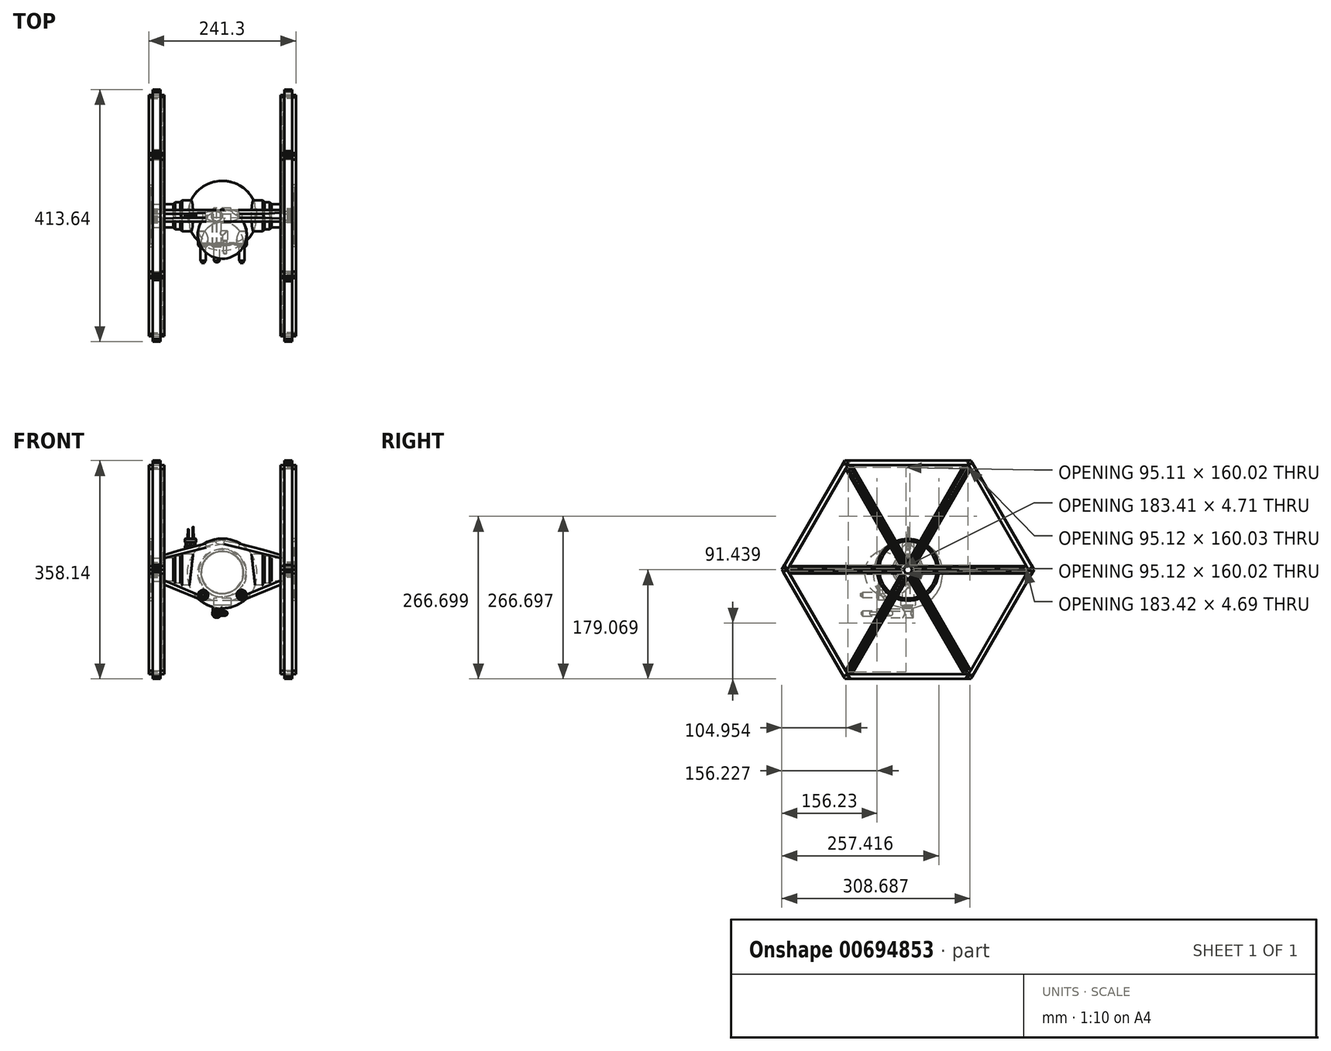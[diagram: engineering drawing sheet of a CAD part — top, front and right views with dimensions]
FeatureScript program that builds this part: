
annotation { "Feature Type Name" : "Feature", "Feature Type Description" : "" }
export const myFeature = defineFeature(function(context is Context, id is Id, definition is map)
    precondition{}
    {
        {
            var Q0;
            Q0=qCreatedBy(makeId("Right.planeOp"),FACE);
            var sketch = newSketch(context, id + "F0", { "sketchPlane" : qUnion([Q0])});
            skLineSegment(sketch, "E0", {"start": v(0, 51.2) * mm, "end": v(0, -63.1) * mm, "construction": true});
            skLineSegment(sketch, "E1", {"start": v(0, 51.2) * mm, "end": v(0, -63.1) * mm});
            skArc(sketch, "E2", {"start": v(0, 51.2) * mm, "mid": v(-57.2, -5.94) * mm, "end": v(0, -63.1) * mm});
            skSolve(sketch);
        }
        {
            var Q0;
            Q0=makeQuery(id+"F0.imprint","IMPRINT",FACE,{"disambiguationData":[TD([[makeQuery(id+"F0.imprint","IMPRINT",EDGE,{"derivedFrom":sQuery(id+"F0.wireOp",EDGE,"E1")}),-1.0]])]});
            var Q1;
            Q1=sQuery(id+"F0.wireOp",EDGE,"E1");
            revolve(context, id + "F1", {"entities" : qUnion([Q0]), "axis" : qUnion([Q1]), "revolveType" : RevolveType.FULL});
        }
        {
            var Q0;
            Q0=qCreatedBy(makeId("Right.planeOp"),FACE);
            var sketch = newSketch(context, id + "F2", { "sketchPlane" : qUnion([Q0])});
            skCircle(sketch, "E3", {"center": v(0, 0) * mm, "radius": 19.05 * mm});
            skSolve(sketch);
        }
        {
            var Q0;
            Q0 = qSketchRegion(id + "F2", true);
            extrude(context, id + "F3", {"entities" : qUnion([Q0]), "operationType" : NewBodyOperationType.ADD, "depth" : 203.2 * mm, "offsetDistance" : 25.4 * mm, "symmetric" : true});
        }
        {
            var Q0;
            Q0=makeQuery(id+"F3.opExtrude","CAP_FACE",FACE,{"disambiguationData":[OSD([sQuery(id+"F2.wireOp",EDGE,"E3")])],"isStart":false});
            var sketch = newSketch(context, id + "F4", { "sketchPlane" : qUnion([Q0])});
            skCircle(sketch, "E4.cCircle", {"center": v(0, 0) * mm, "radius": 171.45 * mm, "construction": true});
            skLineSegment(sketch, "E4.0", {"start": v(-98.99, 171.45) * mm, "end": v(98.99, 171.45) * mm});
            skLineSegment(sketch, "E4.1", {"start": v(98.99, 171.45) * mm, "end": v(197.97, 0) * mm});
            skLineSegment(sketch, "E4.2", {"start": v(197.97, 0) * mm, "end": v(98.99, -171.45) * mm});
            skLineSegment(sketch, "E4.3", {"start": v(98.99, -171.45) * mm, "end": v(-98.99, -171.45) * mm});
            skLineSegment(sketch, "E4.4", {"start": v(-98.99, -171.45) * mm, "end": v(-197.97, 0) * mm});
            skLineSegment(sketch, "E4.5", {"start": v(-197.97, 0) * mm, "end": v(-98.99, 171.45) * mm});
            skPoint(sketch, "E4.0.midPoint", {"position": v(0, 171.45) * mm});
            skSolve(sketch);
        }
        {
            var Q0;
            Q0 = qSketchRegion(id + "F4", true);
            extrude(context, id + "F5", {"entities" : qUnion([Q0]), "depth" : 12.7 * mm, "offsetDistance" : 25.4 * mm});
        }
        {
            var Q0;
            Q0=makeQuery(id+"F3.opExtrude","CAP_FACE",FACE,{"disambiguationData":[OSD([sQuery(id+"F2.wireOp",EDGE,"E3")])],"isStart":true});
            var sketch = newSketch(context, id + "F6", { "sketchPlane" : qUnion([Q0])});
            skCircle(sketch, "E5.cCircle", {"center": v(0, 0) * mm, "radius": 171.45 * mm, "construction": true});
            skLineSegment(sketch, "E5.0", {"start": v(-98.99, 171.45) * mm, "end": v(98.99, 171.45) * mm});
            skLineSegment(sketch, "E5.1", {"start": v(98.99, 171.45) * mm, "end": v(197.97, 0) * mm});
            skLineSegment(sketch, "E5.2", {"start": v(197.97, 0) * mm, "end": v(98.99, -171.45) * mm});
            skLineSegment(sketch, "E5.3", {"start": v(98.99, -171.45) * mm, "end": v(-98.99, -171.45) * mm});
            skLineSegment(sketch, "E5.4", {"start": v(-98.99, -171.45) * mm, "end": v(-197.97, 0) * mm});
            skLineSegment(sketch, "E5.5", {"start": v(-197.97, 0) * mm, "end": v(-98.99, 171.45) * mm});
            skPoint(sketch, "E5.0.midPoint", {"position": v(0, 171.45) * mm});
            skSolve(sketch);
        }
        {
            var Q0;
            Q0=makeQuery(id+"F6.imprint","IMPRINT",FACE,{"disambiguationData":[TD([[makeQuery(id+"F6.imprint","IMPRINT",EDGE,{"derivedFrom":sQuery(id+"F6.wireOp",EDGE,"E5.0")}),-1.0]])]});
            extrude(context, id + "F7", {"entities" : qUnion([Q0]), "depth" : 12.7 * mm, "offsetDistance" : 25.4 * mm});
        }
        {
            var Q0;
            Q0=makeQuery(id+"F3.opExtrude","CAP_FACE",FACE,{"disambiguationData":[OSD([sQuery(id+"F2.wireOp",EDGE,"E3")])],"isStart":true});
            extrude(context, id + "F8", {"entities" : qUnion([Q0]), "depth" : 12.7 * mm, "offsetDistance" : 25.4 * mm});
        }
        {
            var Q0;
            Q0=makeQuery(id+"F5.opExtrude","CAP_FACE",FACE,{"disambiguationData":[OSD([sQuery(id+"F4.wireOp",EDGE,"E4.0"),sQuery(id+"F4.wireOp",EDGE,"E4.1"),sQuery(id+"F4.wireOp",EDGE,"E4.2"),sQuery(id+"F4.wireOp",EDGE,"E4.3"),sQuery(id+"F4.wireOp",EDGE,"E4.4"),sQuery(id+"F4.wireOp",EDGE,"E4.5")])],"isStart":false});
            var sketch = newSketch(context, id + "F9", { "sketchPlane" : qUnion([Q0])});
            skCircle(sketch, "E6", {"center": v(0, 0) * mm, "radius": 19.05 * mm});
            skSolve(sketch);
        }
        {
            var Q0;
            Q0 = qSketchRegion(id + "F9", true);
            extrude(context, id + "F10", {"entities" : qUnion([Q0]), "operationType" : NewBodyOperationType.ADD, "depth" : 0.03 * mm, "offsetDistance" : 25.4 * mm});
        }
        {
            var Q0;
            Q0=qCreatedBy(makeId("Right.planeOp"),FACE);
            var sketch = newSketch(context, id + "F11", { "sketchPlane" : qUnion([Q0])});
            skCircle(sketch, "E7", {"center": v(0, 0) * mm, "radius": 25.4 * mm});
            skSolve(sketch);
        }
        {
            var Q0;
            Q0 = qSketchRegion(id + "F11", true);
            extrude(context, id + "F12", {"entities" : qUnion([Q0]), "operationType" : NewBodyOperationType.ADD, "depth" : 142.24 * mm, "offsetDistance" : 25.4 * mm, "symmetric" : true});
        }
        {
            var Q0;
            Q0=qCreatedBy(makeId("Right.planeOp"),FACE);
            var sketch = newSketch(context, id + "F13", { "sketchPlane" : qUnion([Q0])});
            skCircle(sketch, "E8", {"center": v(0, 0) * mm, "radius": 22.23 * mm});
            skSolve(sketch);
        }
        {
            var Q0;
            Q0 = qSketchRegion(id + "F13", true);
            extrude(context, id + "F14", {"entities" : qUnion([Q0]), "operationType" : NewBodyOperationType.ADD, "depth" : 165.1 * mm, "offsetDistance" : 25.4 * mm, "symmetric" : true});
        }
        {
            var Q0;
            Q0=makeQuery(id+"F10.opExtrude","CAP_FACE",FACE,{"disambiguationData":[OSD([sQuery(id+"F9.wireOp",EDGE,"E6")])],"isStart":false});
            var sketch = newSketch(context, id + "F15", { "sketchPlane" : qUnion([Q0])});
            skCircle(sketch, "E9", {"center": v(0, 0) * mm, "radius": 50.8 * mm});
            skSolve(sketch);
        }
        {
            var Q0;
            Q0 = qSketchRegion(id + "F15", true);
            extrude(context, id + "F16", {"entities" : qUnion([Q0]), "depth" : 8.9 * mm, "offsetDistance" : 25.4 * mm});
        }
        {
            var Q0;
            Q0=makeQuery(id+"F8.opExtrude","CAP_FACE",FACE,{"disambiguationData":[OSD([sQuery(id+"F2.wireOp",EDGE,"E3")])],"isStart":false});
            var sketch = newSketch(context, id + "F17", { "sketchPlane" : qUnion([Q0])});
            skCircle(sketch, "E10", {"center": v(0, 0) * mm, "radius": 50.8 * mm});
            skSolve(sketch);
        }
        {
            var Q0;
            Q0 = qSketchRegion(id + "F17", true);
            extrude(context, id + "F18", {"entities" : qUnion([Q0]), "depth" : 8.9 * mm, "offsetDistance" : 25.4 * mm});
        }
        {
            var Q0;
            Q0=makeQuery(id+"F7.opExtrude","CAP_FACE",FACE,{"disambiguationData":[OSD([sQuery(id+"F2.wireOp",EDGE,"E3"),sQuery(id+"F6.wireOp",EDGE,"E5.0"),sQuery(id+"F6.wireOp",EDGE,"E5.1"),sQuery(id+"F6.wireOp",EDGE,"E5.2"),sQuery(id+"F6.wireOp",EDGE,"E5.3"),sQuery(id+"F6.wireOp",EDGE,"E5.4"),sQuery(id+"F6.wireOp",EDGE,"E5.5")])],"isStart":false});
            var sketch = newSketch(context, id + "F19", { "sketchPlane" : qUnion([Q0])});
            skSolve(sketch);
        }
        {
            var Q0;
            Q0=makeQuery(id+"F19.imprint","IMPRINT",FACE,{"disambiguationData":[TD([[makeQuery(id+"F19.imprint","IMPRINT",EDGE,{"derivedFrom":makeQuery(id+"F7.opExtrude","CAP_EDGE",EDGE,{"disambiguationData":[OSD([sQuery(id+"F6.wireOp",EDGE,"E5.0")])],"isStart":false})}),-1.0]])]});
            var sketch = newSketch(context, id + "F20", { "sketchPlane" : qUnion([Q0])});
            skLineSegment(sketch, "E11", {"start": v(-98.99, 171.45) * mm, "end": v(-102.56, 165.29) * mm});
            skLineSegment(sketch, "E12", {"start": v(-98.99, 171.45) * mm, "end": v(-91.87, 171.45) * mm});
            skLineSegment(sketch, "E13", {"start": v(98.99, -171.45) * mm, "end": v(102.55, -165.29) * mm});
            skLineSegment(sketch, "E14", {"start": v(98.99, -171.45) * mm, "end": v(91.87, -171.45) * mm});
            skLineSegment(sketch, "E15", {"start": v(91.87, -171.45) * mm, "end": v(-102.56, 165.29) * mm});
            skLineSegment(sketch, "E16", {"start": v(-91.87, 171.45) * mm, "end": v(102.55, -165.29) * mm});
            skLineSegment(sketch, "E17", {"start": v(98.99, 171.45) * mm, "end": v(91.87, 171.45) * mm});
            skLineSegment(sketch, "E18", {"start": v(98.99, 171.45) * mm, "end": v(102.55, 165.29) * mm});
            skLineSegment(sketch, "E19", {"start": v(-98.99, -171.45) * mm, "end": v(-102.54, -165.29) * mm});
            skLineSegment(sketch, "E20", {"start": v(-98.99, -171.45) * mm, "end": v(-91.87, -171.45) * mm});
            skLineSegment(sketch, "E21", {"start": v(-91.87, -171.45) * mm, "end": v(102.55, 165.29) * mm});
            skLineSegment(sketch, "E22", {"start": v(91.87, 171.45) * mm, "end": v(-102.54, -165.29) * mm});
            skLineSegment(sketch, "E23", {"start": v(197.97, 0) * mm, "end": v(194.4, 6.16) * mm});
            skLineSegment(sketch, "E24", {"start": v(197.97, 0) * mm, "end": v(194.43, -6.16) * mm});
            skLineSegment(sketch, "E25", {"start": v(-197.98, 0) * mm, "end": v(-194.43, 6.15) * mm});
            skLineSegment(sketch, "E26", {"start": v(-197.98, 0) * mm, "end": v(-194.42, -6.15) * mm});
            skLineSegment(sketch, "E27", {"start": v(-194.43, 6.15) * mm, "end": v(194.4, 6.16) * mm});
            skLineSegment(sketch, "E28", {"start": v(194.43, -6.16) * mm, "end": v(-194.42, -6.15) * mm});
            skSolve(sketch);
        }
        {
            var Q0;
            Q0 = qSketchRegion(id + "F20", true);
            extrude(context, id + "F21", {"entities" : qUnion([Q0]), "depth" : 38.1 * mm, "offsetDistance" : 25.4 * mm, "symmetric" : true});
        }
        {
            var Q0;
            Q0=makeQuery(id+"F5.opExtrude","CAP_FACE",FACE,{"disambiguationData":[OSD([sQuery(id+"F4.wireOp",EDGE,"E4.0"),sQuery(id+"F4.wireOp",EDGE,"E4.1"),sQuery(id+"F4.wireOp",EDGE,"E4.2"),sQuery(id+"F4.wireOp",EDGE,"E4.3"),sQuery(id+"F4.wireOp",EDGE,"E4.4"),sQuery(id+"F4.wireOp",EDGE,"E4.5")])],"isStart":false});
            var sketch = newSketch(context, id + "F22", { "sketchPlane" : qUnion([Q0])});
            skLineSegment(sketch, "E29", {"start": v(-98.99, 171.45) * mm, "end": v(-102.54, 165.3) * mm});
            skLineSegment(sketch, "E30", {"start": v(-98.99, 171.45) * mm, "end": v(-91.87, 171.45) * mm});
            skLineSegment(sketch, "E31", {"start": v(98.99, 171.45) * mm, "end": v(91.88, 171.45) * mm});
            skLineSegment(sketch, "E32", {"start": v(98.99, 171.45) * mm, "end": v(102.55, 165.28) * mm});
            skLineSegment(sketch, "E33", {"start": v(197.97, 0) * mm, "end": v(194.42, 6.16) * mm});
            skLineSegment(sketch, "E34", {"start": v(197.97, 0) * mm, "end": v(194.42, -6.16) * mm});
            skLineSegment(sketch, "E35", {"start": v(98.99, -171.45) * mm, "end": v(102.54, -165.29) * mm});
            skLineSegment(sketch, "E36", {"start": v(98.99, -171.45) * mm, "end": v(91.86, -171.45) * mm});
            skLineSegment(sketch, "E37", {"start": v(-98.99, -171.45) * mm, "end": v(-91.88, -171.45) * mm});
            skLineSegment(sketch, "E38", {"start": v(-98.99, -171.45) * mm, "end": v(-102.54, -165.3) * mm});
            skLineSegment(sketch, "E39", {"start": v(-197.97, 0) * mm, "end": v(-194.42, 6.16) * mm});
            skLineSegment(sketch, "E40", {"start": v(-197.97, 0) * mm, "end": v(-194.42, -6.16) * mm});
            skLineSegment(sketch, "E41", {"start": v(-194.42, -6.16) * mm, "end": v(194.42, -6.16) * mm});
            skLineSegment(sketch, "E42", {"start": v(194.42, 6.16) * mm, "end": v(-194.42, 6.16) * mm});
            skLineSegment(sketch, "E43", {"start": v(-102.54, 165.3) * mm, "end": v(91.86, -171.45) * mm});
            skLineSegment(sketch, "E44", {"start": v(-91.87, 171.45) * mm, "end": v(102.54, -165.29) * mm});
            skLineSegment(sketch, "E45", {"start": v(91.88, 171.45) * mm, "end": v(-102.54, -165.3) * mm});
            skLineSegment(sketch, "E46", {"start": v(102.55, 165.28) * mm, "end": v(-91.88, -171.45) * mm});
            skSolve(sketch);
        }
        {
            var Q0;
            Q0 = qSketchRegion(id + "F22", true);
            extrude(context, id + "F23", {"entities" : qUnion([Q0]), "depth" : 38.1 * mm, "offsetDistance" : 25.4 * mm, "symmetric" : true});
        }
        {
            var Q0;
            Q0=makeQuery(id+"F23.opExtrude","CAP_FACE",FACE,{"disambiguationData":[OSD([sQuery(id+"F22.wireOp",EDGE,"E29"),sQuery(id+"F22.wireOp",EDGE,"E30"),sQuery(id+"F22.wireOp",EDGE,"E31"),sQuery(id+"F22.wireOp",EDGE,"E32"),sQuery(id+"F22.wireOp",EDGE,"E33"),sQuery(id+"F22.wireOp",EDGE,"E34"),sQuery(id+"F22.wireOp",EDGE,"E35"),sQuery(id+"F22.wireOp",EDGE,"E36"),sQuery(id+"F22.wireOp",EDGE,"E37"),sQuery(id+"F22.wireOp",EDGE,"E38"),sQuery(id+"F22.wireOp",EDGE,"E39"),sQuery(id+"F22.wireOp",EDGE,"E40"),sQuery(id+"F22.wireOp",EDGE,"E41"),sQuery(id+"F22.wireOp",EDGE,"E42"),sQuery(id+"F22.wireOp",EDGE,"E43"),sQuery(id+"F22.wireOp",EDGE,"E44"),sQuery(id+"F22.wireOp",EDGE,"E45"),sQuery(id+"F22.wireOp",EDGE,"E46")])],"isStart":false});
            var sketch = newSketch(context, id + "F24", { "sketchPlane" : qUnion([Q0])});
            skLineSegment(sketch, "E47.bottom", {"start": v(-254.73, 221.4) * mm, "end": v(358.63, 221.4) * mm});
            skLineSegment(sketch, "E47.top", {"start": v(-254.73, -186.2) * mm, "end": v(358.63, -186.2) * mm});
            skLineSegment(sketch, "E47.left", {"start": v(-254.73, 221.4) * mm, "end": v(-254.73, -186.2) * mm});
            skLineSegment(sketch, "E47.right", {"start": v(358.63, 221.4) * mm, "end": v(358.63, -186.2) * mm});
            skSolve(sketch);
        }
        {
            var Q0;
            Q0 = qSketchRegion(id + "F24", true);
            extrude(context, id + "F25", {"entities" : qUnion([Q0]), "operationType" : NewBodyOperationType.REMOVE, "depth" : 25.4 * mm, "offsetDistance" : 25.4 * mm, "symmetric" : true});
        }
        {
            var Q0;
            Q0=makeQuery(id+"F21.opExtrude","CAP_FACE",FACE,{"disambiguationData":[OSD([sQuery(id+"F20.wireOp",EDGE,"E11"),sQuery(id+"F20.wireOp",EDGE,"E12"),sQuery(id+"F20.wireOp",EDGE,"E13"),sQuery(id+"F20.wireOp",EDGE,"E14"),sQuery(id+"F20.wireOp",EDGE,"E15"),sQuery(id+"F20.wireOp",EDGE,"E16"),sQuery(id+"F20.wireOp",EDGE,"E17"),sQuery(id+"F20.wireOp",EDGE,"E18"),sQuery(id+"F20.wireOp",EDGE,"E19"),sQuery(id+"F20.wireOp",EDGE,"E20"),sQuery(id+"F20.wireOp",EDGE,"E21"),sQuery(id+"F20.wireOp",EDGE,"E22"),sQuery(id+"F20.wireOp",EDGE,"E23"),sQuery(id+"F20.wireOp",EDGE,"E24"),sQuery(id+"F20.wireOp",EDGE,"E25"),sQuery(id+"F20.wireOp",EDGE,"E26"),sQuery(id+"F20.wireOp",EDGE,"E27"),sQuery(id+"F20.wireOp",EDGE,"E28")])],"isStart":false});
            var sketch = newSketch(context, id + "F26", { "sketchPlane" : qUnion([Q0])});
            skLineSegment(sketch, "E48.bottom", {"start": v(-248.69, 213.9) * mm, "end": v(348.05, 213.9) * mm});
            skLineSegment(sketch, "E48.top", {"start": v(-248.69, -200.94) * mm, "end": v(348.05, -200.94) * mm});
            skLineSegment(sketch, "E48.left", {"start": v(-248.69, 213.9) * mm, "end": v(-248.69, -200.94) * mm});
            skLineSegment(sketch, "E48.right", {"start": v(348.05, 213.9) * mm, "end": v(348.05, -200.94) * mm});
            skSolve(sketch);
        }
        {
            var Q0;
            Q0 = qSketchRegion(id + "F26", true);
            extrude(context, id + "F27", {"entities" : qUnion([Q0]), "operationType" : NewBodyOperationType.REMOVE, "depth" : 25.4 * mm, "offsetDistance" : 25.4 * mm, "symmetric" : true});
        }
        {
            var Q0;
            Q0=makeQuery(id+"F7.opExtrude","SWEPT_FACE",FACE,{"disambiguationData":[OSD([sQuery(id+"F6.wireOp",EDGE,"E5.0")])]});
            var sketch = newSketch(context, id + "F28", { "sketchPlane" : qUnion([Q0])});
            skLineSegment(sketch, "E49.bottom", {"start": v(-114.3, 98.99) * mm, "end": v(-101.6, 98.99) * mm});
            skLineSegment(sketch, "E49.top", {"start": v(-114.3, -98.99) * mm, "end": v(-101.6, -98.99) * mm});
            skLineSegment(sketch, "E49.left", {"start": v(-114.3, 98.99) * mm, "end": v(-114.3, -98.99) * mm});
            skLineSegment(sketch, "E49.right", {"start": v(-101.6, 98.99) * mm, "end": v(-101.6, -98.99) * mm});
            skLineSegment(sketch, "E50.bottom", {"start": v(101.63, 98.98) * mm, "end": v(114.3, 98.98) * mm});
            skLineSegment(sketch, "E50.top", {"start": v(101.63, -98.98) * mm, "end": v(114.3, -98.98) * mm});
            skLineSegment(sketch, "E50.left", {"start": v(101.63, 98.98) * mm, "end": v(101.63, -98.98) * mm});
            skLineSegment(sketch, "E50.right", {"start": v(114.3, 98.98) * mm, "end": v(114.3, -98.98) * mm});
            skSolve(sketch);
        }
        {
            var Q0;
            Q0=makeQuery(id+"F7.opExtrude","SWEPT_FACE",FACE,{"disambiguationData":[OSD([sQuery(id+"F6.wireOp",EDGE,"E5.5")])]});
            var sketch = newSketch(context, id + "F29", { "sketchPlane" : qUnion([Q0])});
            skLineSegment(sketch, "E51.bottom", {"start": v(114.3, -98.99) * mm, "end": v(101.6, -98.99) * mm});
            skLineSegment(sketch, "E51.top", {"start": v(114.3, 98.99) * mm, "end": v(101.6, 98.99) * mm});
            skLineSegment(sketch, "E51.left", {"start": v(114.3, -98.99) * mm, "end": v(114.3, 98.99) * mm});
            skLineSegment(sketch, "E51.right", {"start": v(101.6, -98.99) * mm, "end": v(101.6, 98.99) * mm});
            skLineSegment(sketch, "E52.bottom", {"start": v(-101.59, -98.99) * mm, "end": v(-114.27, -98.99) * mm});
            skLineSegment(sketch, "E52.top", {"start": v(-101.59, 98.99) * mm, "end": v(-114.27, 98.99) * mm});
            skLineSegment(sketch, "E52.left", {"start": v(-101.59, -98.99) * mm, "end": v(-101.59, 98.99) * mm});
            skLineSegment(sketch, "E52.right", {"start": v(-114.27, -98.99) * mm, "end": v(-114.27, 98.99) * mm});
            skSolve(sketch);
        }
        {
            var Q0;
            Q0=makeQuery(id+"F5.opExtrude","SWEPT_FACE",FACE,{"disambiguationData":[OSD([sQuery(id+"F4.wireOp",EDGE,"E4.2")])]});
            var sketch = newSketch(context, id + "F30", { "sketchPlane" : qUnion([Q0])});
            skLineSegment(sketch, "E53.bottom", {"start": v(-114.3, 98.99) * mm, "end": v(-101.6, 98.99) * mm});
            skLineSegment(sketch, "E53.top", {"start": v(-114.3, -98.99) * mm, "end": v(-101.6, -98.99) * mm});
            skLineSegment(sketch, "E53.left", {"start": v(-114.3, 98.99) * mm, "end": v(-114.3, -98.99) * mm});
            skLineSegment(sketch, "E53.right", {"start": v(-101.6, 98.99) * mm, "end": v(-101.6, -98.99) * mm});
            skLineSegment(sketch, "E54.bottom", {"start": v(101.59, 98.99) * mm, "end": v(114.3, 98.99) * mm});
            skLineSegment(sketch, "E54.top", {"start": v(101.59, -98.99) * mm, "end": v(114.3, -98.99) * mm});
            skLineSegment(sketch, "E54.left", {"start": v(101.59, 98.99) * mm, "end": v(101.59, -98.99) * mm});
            skLineSegment(sketch, "E54.right", {"start": v(114.3, 98.99) * mm, "end": v(114.3, -98.99) * mm});
            skSolve(sketch);
        }
        {
            var Q0;
            Q0=makeQuery(id+"F7.opExtrude","SWEPT_FACE",FACE,{"disambiguationData":[OSD([sQuery(id+"F6.wireOp",EDGE,"E5.3")])]});
            var sketch = newSketch(context, id + "F31", { "sketchPlane" : qUnion([Q0])});
            skLineSegment(sketch, "E55.bottom", {"start": v(-114.3, 98.99) * mm, "end": v(-101.6, 98.99) * mm});
            skLineSegment(sketch, "E55.top", {"start": v(-114.3, -98.99) * mm, "end": v(-101.6, -98.99) * mm});
            skLineSegment(sketch, "E55.left", {"start": v(-114.3, 98.99) * mm, "end": v(-114.3, -98.99) * mm});
            skLineSegment(sketch, "E55.right", {"start": v(-101.6, 98.99) * mm, "end": v(-101.6, -98.99) * mm});
            skLineSegment(sketch, "E56.bottom", {"start": v(101.62, 98.99) * mm, "end": v(114.3, 98.99) * mm});
            skLineSegment(sketch, "E56.top", {"start": v(101.62, -98.99) * mm, "end": v(114.3, -98.99) * mm});
            skLineSegment(sketch, "E56.left", {"start": v(101.62, 98.99) * mm, "end": v(101.62, -98.99) * mm});
            skLineSegment(sketch, "E56.right", {"start": v(114.3, 98.99) * mm, "end": v(114.3, -98.99) * mm});
            skSolve(sketch);
        }
        {
            var Q0;
            Q0=makeQuery(id+"F7.opExtrude","SWEPT_FACE",FACE,{"disambiguationData":[OSD([sQuery(id+"F6.wireOp",EDGE,"E5.2")])]});
            var sketch = newSketch(context, id + "F32", { "sketchPlane" : qUnion([Q0])});
            skLineSegment(sketch, "E57.bottom", {"start": v(-114.3, 98.99) * mm, "end": v(-101.6, 98.99) * mm});
            skLineSegment(sketch, "E57.top", {"start": v(-114.3, -98.99) * mm, "end": v(-101.6, -98.99) * mm});
            skLineSegment(sketch, "E57.left", {"start": v(-114.3, 98.99) * mm, "end": v(-114.3, -98.99) * mm});
            skLineSegment(sketch, "E57.right", {"start": v(-101.6, 98.99) * mm, "end": v(-101.6, -98.99) * mm});
            skLineSegment(sketch, "E58.bottom", {"start": v(101.6, 98.99) * mm, "end": v(114.3, 98.99) * mm});
            skLineSegment(sketch, "E58.top", {"start": v(101.6, -98.99) * mm, "end": v(114.3, -98.99) * mm});
            skLineSegment(sketch, "E58.left", {"start": v(101.6, 98.99) * mm, "end": v(101.6, -98.99) * mm});
            skLineSegment(sketch, "E58.right", {"start": v(114.3, 98.99) * mm, "end": v(114.3, -98.99) * mm});
            skSolve(sketch);
        }
        {
            var Q0;
            Q0=makeQuery(id+"F7.opExtrude","SWEPT_FACE",FACE,{"disambiguationData":[OSD([sQuery(id+"F6.wireOp",EDGE,"E5.1")])]});
            var sketch = newSketch(context, id + "F33", { "sketchPlane" : qUnion([Q0])});
            skLineSegment(sketch, "E59.bottom", {"start": v(-114.3, 98.99) * mm, "end": v(-101.6, 98.99) * mm});
            skLineSegment(sketch, "E59.top", {"start": v(-114.3, -98.99) * mm, "end": v(-101.6, -98.99) * mm});
            skLineSegment(sketch, "E59.left", {"start": v(-114.3, 98.99) * mm, "end": v(-114.3, -98.99) * mm});
            skLineSegment(sketch, "E59.right", {"start": v(-101.6, 98.99) * mm, "end": v(-101.6, -98.99) * mm});
            skLineSegment(sketch, "E60.bottom", {"start": v(101.61, 98.99) * mm, "end": v(114.37, 98.99) * mm});
            skLineSegment(sketch, "E60.top", {"start": v(101.61, -98.99) * mm, "end": v(114.37, -98.99) * mm});
            skLineSegment(sketch, "E60.left", {"start": v(101.61, 98.99) * mm, "end": v(101.61, -98.99) * mm});
            skLineSegment(sketch, "E60.right", {"start": v(114.37, 98.99) * mm, "end": v(114.37, -98.99) * mm});
            skSolve(sketch);
        }
        {
            var Q0;
            Q0 = qSketchRegion(id + "F33", true);
            extrude(context, id + "F34", {"entities" : qUnion([Q0]), "depth" : 7.62 * mm, "offsetDistance" : 25.4 * mm});
        }
        {
            var Q0;
            Q0 = qSketchRegion(id + "F32", true);
            extrude(context, id + "F35", {"entities" : qUnion([Q0]), "depth" : 7.62 * mm, "offsetDistance" : 25.4 * mm});
        }
        {
            var Q0;
            Q0 = qSketchRegion(id + "F31", true);
            extrude(context, id + "F36", {"entities" : qUnion([Q0]), "depth" : 7.62 * mm, "offsetDistance" : 25.4 * mm});
        }
        {
            var Q0;
            Q0 = qSketchRegion(id + "F30", true);
            extrude(context, id + "F37", {"entities" : qUnion([Q0]), "depth" : 7.62 * mm, "offsetDistance" : 25.4 * mm});
        }
        {
            var Q0;
            Q0 = qSketchRegion(id + "F29", true);
            extrude(context, id + "F38", {"entities" : qUnion([Q0]), "depth" : 7.62 * mm, "offsetDistance" : 25.4 * mm});
        }
        {
            var Q0;
            Q0 = qSketchRegion(id + "F28", true);
            extrude(context, id + "F39", {"entities" : qUnion([Q0]), "depth" : 7.62 * mm, "offsetDistance" : 25.4 * mm});
        }
        {
            var Q0;
            Q0=qCreatedBy(makeId("Front.planeOp"),FACE);
            cPlane(context, id + "F40", {"entities" : qUnion([Q0]), "cplaneType" : CPlaneType.OFFSET, "offset" : 38.1 * mm, "width" : 152.4 * mm, "height" : 152.4 * mm});
        }
        {
            var Q0;
            Q0=qCreatedBy(id+"F40.planeOp",FACE);
            var sketch = newSketch(context, id + "F41", { "sketchPlane" : qUnion([Q0])});
            skCircle(sketch, "E61", {"center": v(-31.2, -41.21) * mm, "radius": 8.26 * mm});
            skCircle(sketch, "E62", {"center": v(31.77, -41.21) * mm, "radius": 8.26 * mm});
            skSolve(sketch);
        }
        {
            var Q0;
            Q0 = qSketchRegion(id + "F41", true);
            extrude(context, id + "F42", {"entities" : qUnion([Q0]), "operationType" : NewBodyOperationType.ADD, "depth" : 25.4 * mm, "offsetDistance" : 25.4 * mm, "symmetric" : true});
        }
        {
            var Q0;
            Q0=makeQuery(id+"F42.opExtrude","CAP_FACE",FACE,{"disambiguationData":[OSD([sQuery(id+"F41.wireOp",EDGE,"E61")])],"isStart":false});
            var sketch = newSketch(context, id + "F43", { "sketchPlane" : qUnion([Q0])});
            skCircle(sketch, "E63", {"center": v(-31.2, -41.21) * mm, "radius": 4.45 * mm});
            skSolve(sketch);
        }
        {
            var Q0;
            Q0=makeQuery(id+"F42.opExtrude","CAP_FACE",FACE,{"disambiguationData":[OSD([sQuery(id+"F41.wireOp",EDGE,"E62")])],"isStart":false});
            var sketch = newSketch(context, id + "F44", { "sketchPlane" : qUnion([Q0])});
            skCircle(sketch, "E64", {"center": v(31.77, -41.21) * mm, "radius": 4.45 * mm});
            skSolve(sketch);
        }
        {
            var Q0;
            Q0 = qSketchRegion(id + "F44", true);
            extrude(context, id + "F45", {"entities" : qUnion([Q0]), "operationType" : NewBodyOperationType.ADD, "depth" : 25.4 * mm, "offsetDistance" : 25.4 * mm});
        }
        {
            var Q0;
            Q0 = qSketchRegion(id + "F43", true);
            extrude(context, id + "F46", {"entities" : qUnion([Q0]), "operationType" : NewBodyOperationType.ADD, "depth" : 25.4 * mm, "offsetDistance" : 25.4 * mm});
        }
        {
            var Q0;
            Q0=makeQuery(id+"F46.opExtrude","CAP_FACE",FACE,{"disambiguationData":[OSD([sQuery(id+"F43.wireOp",EDGE,"E63")])],"isStart":false});
            var sketch = newSketch(context, id + "F47", { "sketchPlane" : qUnion([Q0])});
            skCircle(sketch, "E65", {"center": v(-31.2, -41.21) * mm, "radius": 2.54 * mm});
            skSolve(sketch);
        }
        {
            var Q0;
            Q0=makeQuery(id+"F45.opExtrude","CAP_FACE",FACE,{"disambiguationData":[OSD([sQuery(id+"F44.wireOp",EDGE,"E64")])],"isStart":false});
            var sketch = newSketch(context, id + "F48", { "sketchPlane" : qUnion([Q0])});
            skCircle(sketch, "E66", {"center": v(31.77, -41.21) * mm, "radius": 2.54 * mm});
            skSolve(sketch);
        }
        {
            var Q0;
            Q0 = qSketchRegion(id + "F48", true);
            var Q1;
            Q1=makeQuery(id+"F47.imprint","IMPRINT",FACE,{"disambiguationData":[TD([[makeQuery(id+"F47.imprint","IMPRINT",EDGE,{"derivedFrom":sQuery(id+"F47.wireOp",EDGE,"E65")}),1.0]])]});
            extrude(context, id + "F49", {"entities" : qUnion([Q0, Q1]), "depth" : 1.27 * mm, "offsetDistance" : 25.4 * mm});
        }
        {
            var Q0;
            Q0=makeQuery(id+"F42.opExtrude","CAP_EDGE",EDGE,{"disambiguationData":[OSD([sQuery(id+"F41.wireOp",EDGE,"E61")])],"isStart":false});
            var Q1;
            Q1=makeQuery(id+"F46.opExtrude","CAP_EDGE",EDGE,{"disambiguationData":[OSD([sQuery(id+"F43.wireOp",EDGE,"E63")])],"isStart":false});
            var Q2;
            Q2=makeQuery(id+"F42.opExtrude","CAP_EDGE",EDGE,{"disambiguationData":[OSD([sQuery(id+"F41.wireOp",EDGE,"E62")])],"isStart":false});
            var Q3;
            Q3=makeQuery(id+"F45.opExtrude","CAP_EDGE",EDGE,{"disambiguationData":[OSD([sQuery(id+"F44.wireOp",EDGE,"E64")])],"isStart":false});
            chamfer(context, id + "F50", {"entities" : qUnion([Q0, Q1, Q2, Q3]), "width" : 2.54 * mm, "tangentPropagation" : true});
        }
        {
            var Q0;
            Q0=qCreatedBy(makeId("Front.planeOp"),FACE);
            var sketch = newSketch(context, id + "F51", { "sketchPlane" : qUnion([Q0])});
            skLineSegment(sketch, "E67.bottom", {"start": v(0, 50.8) * mm, "end": v(-95.25, 50.8) * mm});
            skLineSegment(sketch, "E67.top", {"start": v(0, 0) * mm, "end": v(-95.25, 0) * mm});
            skLineSegment(sketch, "E67.left", {"start": v(0, 50.8) * mm, "end": v(0, 0) * mm});
            skLineSegment(sketch, "E67.right", {"start": v(-95.25, 50.8) * mm, "end": v(-95.25, 0) * mm});
            skLineSegment(sketch, "E68.bottom", {"start": v(0, 0) * mm, "end": v(95.25, 0) * mm});
            skLineSegment(sketch, "E68.top", {"start": v(0, 50.8) * mm, "end": v(95.25, 50.8) * mm});
            skLineSegment(sketch, "E68.left", {"start": v(0, 0) * mm, "end": v(0, 50.8) * mm});
            skLineSegment(sketch, "E68.right", {"start": v(95.25, 0) * mm, "end": v(95.25, 50.8) * mm});
            skLineSegment(sketch, "E69.top", {"start": v(0, -50.8) * mm, "end": v(-95.25, -50.8) * mm});
            skLineSegment(sketch, "E69.left", {"start": v(0, 0) * mm, "end": v(0, -50.8) * mm});
            skLineSegment(sketch, "E69.right", {"start": v(-95.25, 0) * mm, "end": v(-95.25, -50.8) * mm});
            skLineSegment(sketch, "E70.top", {"start": v(0, -50.8) * mm, "end": v(95.25, -50.8) * mm});
            skLineSegment(sketch, "E70.right", {"start": v(95.25, 0) * mm, "end": v(95.25, -50.8) * mm});
            skSolve(sketch);
        }
        {
            var Q0;
            Q0 = qSketchRegion(id + "F51", true);
            extrude(context, id + "F52", {"entities" : qUnion([Q0]), "depth" : 19.05 * mm, "offsetDistance" : 25.4 * mm, "symmetric" : true});
        }
        {
            var Q0;
            Q0=makeQuery(id+"F52.opExtrude","SWEPT_EDGE",EDGE,{"disambiguationData":[OSD([sQuery(id+"F51.wireOp",EDGE,"E67.bottom"),sQuery(id+"F51.wireOp",EDGE,"E67.right")])]});
            var Q1;
            Q1=makeQuery(id+"F52.opExtrude","SWEPT_EDGE",EDGE,{"disambiguationData":[OSD([sQuery(id+"F51.wireOp",EDGE,"E68.top"),sQuery(id+"F51.wireOp",EDGE,"E68.right")])]});
            var Q2;
            Q2=makeQuery(id+"F52.opExtrude","SWEPT_EDGE",EDGE,{"disambiguationData":[OSD([sQuery(id+"F51.wireOp",EDGE,"E69.top"),sQuery(id+"F51.wireOp",EDGE,"E69.right")])]});
            var Q3;
            Q3=makeQuery(id+"F52.opExtrude","SWEPT_EDGE",EDGE,{"disambiguationData":[OSD([sQuery(id+"F51.wireOp",EDGE,"E70.top"),sQuery(id+"F51.wireOp",EDGE,"E70.right")])]});
            chamfer(context, id + "F53", {"entities" : qUnion([Q0, Q1, Q2, Q3]), "width" : 25.4 * mm, "tangentPropagation" : true});
        }
        {
            var Q0;
            {var subQ0=sQuery(id+"F51.wireOp",EDGE,"E67.bottom");Q0=makeQuery(id+"F53.opChamfer","BLEND_EDGE",EDGE,{"blendedFrom":[makeQuery(id+"F52.opExtrude","SWEPT_EDGE",EDGE,{"disambiguationData":[OSD([subQ0,sQuery(id+"F51.wireOp",EDGE,"E67.right")])]}),makeQuery(id+"F52.opExtrude","SWEPT_FACE",FACE,{"disambiguationData":[OSD([subQ0,sQuery(id+"F51.wireOp",EDGE,"E68.top")])]})],"blendedInto":[makeQuery(id+"F52.opExtrude","SWEPT_FACE",FACE,{"disambiguationData":[OSD([subQ0,sQuery(id+"F51.wireOp",EDGE,"E68.top")])]})]});}
            var Q1;
            {var subQ0=sQuery(id+"F51.wireOp",EDGE,"E68.top");Q1=makeQuery(id+"F53.opChamfer","BLEND_EDGE",EDGE,{"blendedFrom":[makeQuery(id+"F52.opExtrude","SWEPT_EDGE",EDGE,{"disambiguationData":[OSD([subQ0,sQuery(id+"F51.wireOp",EDGE,"E68.right")])]}),makeQuery(id+"F52.opExtrude","SWEPT_FACE",FACE,{"disambiguationData":[OSD([sQuery(id+"F51.wireOp",EDGE,"E67.bottom"),subQ0])]})],"blendedInto":[makeQuery(id+"F52.opExtrude","SWEPT_FACE",FACE,{"disambiguationData":[OSD([sQuery(id+"F51.wireOp",EDGE,"E67.bottom"),subQ0])]})]});}
            var Q2;
            {var subQ0=sQuery(id+"F51.wireOp",EDGE,"E69.top");Q2=makeQuery(id+"F53.opChamfer","BLEND_EDGE",EDGE,{"blendedFrom":[makeQuery(id+"F52.opExtrude","SWEPT_EDGE",EDGE,{"disambiguationData":[OSD([subQ0,sQuery(id+"F51.wireOp",EDGE,"E69.right")])]}),makeQuery(id+"F52.opExtrude","SWEPT_FACE",FACE,{"disambiguationData":[OSD([subQ0,sQuery(id+"F51.wireOp",EDGE,"E70.top")])]})],"blendedInto":[makeQuery(id+"F52.opExtrude","SWEPT_FACE",FACE,{"disambiguationData":[OSD([subQ0,sQuery(id+"F51.wireOp",EDGE,"E70.top")])]})]});}
            var Q3;
            {var subQ0=sQuery(id+"F51.wireOp",EDGE,"E70.top");Q3=makeQuery(id+"F53.opChamfer","BLEND_EDGE",EDGE,{"blendedFrom":[makeQuery(id+"F52.opExtrude","SWEPT_EDGE",EDGE,{"disambiguationData":[OSD([subQ0,sQuery(id+"F51.wireOp",EDGE,"E70.right")])]}),makeQuery(id+"F52.opExtrude","SWEPT_FACE",FACE,{"disambiguationData":[OSD([sQuery(id+"F51.wireOp",EDGE,"E69.top"),subQ0])]})],"blendedInto":[makeQuery(id+"F52.opExtrude","SWEPT_FACE",FACE,{"disambiguationData":[OSD([sQuery(id+"F51.wireOp",EDGE,"E69.top"),subQ0])]})]});}
            chamfer(context, id + "F54", {"entities" : qUnion([Q0, Q1, Q2, Q3]), "width" : 38.1 * mm, "tangentPropagation" : true});
        }
        {
            var Q0;
            {var subQ0=sQuery(id+"F51.wireOp",EDGE,"E67.bottom");var subQ1=makeQuery(id+"F52.opExtrude","SWEPT_FACE",FACE,{"disambiguationData":[OSD([subQ0,sQuery(id+"F51.wireOp",EDGE,"E68.top")])]});Q0=makeQuery(id+"F54.opChamfer","BLEND_EDGE",EDGE,{"blendedFrom":[makeQuery(id+"F53.opChamfer","BLEND_EDGE",EDGE,{"blendedFrom":[makeQuery(id+"F52.opExtrude","SWEPT_EDGE",EDGE,{"disambiguationData":[OSD([subQ0,sQuery(id+"F51.wireOp",EDGE,"E67.right")])]}),subQ1],"blendedInto":[subQ1]}),subQ1],"blendedInto":[subQ1]});}
            var Q1;
            {var subQ0=sQuery(id+"F51.wireOp",EDGE,"E68.top");var subQ1=makeQuery(id+"F52.opExtrude","SWEPT_FACE",FACE,{"disambiguationData":[OSD([sQuery(id+"F51.wireOp",EDGE,"E67.bottom"),subQ0])]});Q1=makeQuery(id+"F54.opChamfer","BLEND_EDGE",EDGE,{"blendedFrom":[makeQuery(id+"F53.opChamfer","BLEND_EDGE",EDGE,{"blendedFrom":[makeQuery(id+"F52.opExtrude","SWEPT_EDGE",EDGE,{"disambiguationData":[OSD([subQ0,sQuery(id+"F51.wireOp",EDGE,"E68.right")])]}),subQ1],"blendedInto":[subQ1]}),subQ1],"blendedInto":[subQ1]});}
            chamfer(context, id + "F55", {"entities" : qUnion([Q0, Q1]), "width" : 44.45 * mm, "tangentPropagation" : true});
        }
        {
            var Q0;
            {var subQ0=sQuery(id+"F51.wireOp",EDGE,"E68.top");var subQ1=sQuery(id+"F51.wireOp",EDGE,"E67.right");var subQ2=sQuery(id+"F51.wireOp",EDGE,"E67.bottom");var subQ3=makeQuery(id+"F52.opExtrude","SWEPT_FACE",FACE,{"disambiguationData":[OSD([subQ2,subQ0])]});Q0=makeQuery(id+"F55.opChamfer","BLEND_EDGE",EDGE,{"blendedFrom":[makeQuery(id+"F54.opChamfer","BLEND_EDGE",EDGE,{"blendedFrom":[makeQuery(id+"F53.opChamfer","BLEND_EDGE",EDGE,{"blendedFrom":[makeQuery(id+"F52.opExtrude","SWEPT_EDGE",EDGE,{"disambiguationData":[OSD([subQ2,subQ1])]}),subQ3],"blendedInto":[subQ3]}),subQ3],"blendedInto":[subQ3]}),makeQuery(id+"F54.opChamfer","BLEND_FACE",FACE,{"disambiguationData":[OSD([subQ2,subQ1,subQ0])]})],"blendedInto":[makeQuery(id+"F54.opChamfer","BLEND_FACE",FACE,{"disambiguationData":[OSD([subQ2,subQ1,subQ0])]})]});}
            var Q1;
            {var subQ0=sQuery(id+"F51.wireOp",EDGE,"E68.right");var subQ1=sQuery(id+"F51.wireOp",EDGE,"E68.top");var subQ2=sQuery(id+"F51.wireOp",EDGE,"E67.bottom");var subQ3=makeQuery(id+"F52.opExtrude","SWEPT_FACE",FACE,{"disambiguationData":[OSD([subQ2,subQ1])]});Q1=makeQuery(id+"F55.opChamfer","BLEND_EDGE",EDGE,{"blendedFrom":[makeQuery(id+"F54.opChamfer","BLEND_EDGE",EDGE,{"blendedFrom":[makeQuery(id+"F53.opChamfer","BLEND_EDGE",EDGE,{"blendedFrom":[makeQuery(id+"F52.opExtrude","SWEPT_EDGE",EDGE,{"disambiguationData":[OSD([subQ1,subQ0])]}),subQ3],"blendedInto":[subQ3]}),subQ3],"blendedInto":[subQ3]}),makeQuery(id+"F54.opChamfer","BLEND_FACE",FACE,{"disambiguationData":[OSD([subQ2,subQ1,subQ0])]})],"blendedInto":[makeQuery(id+"F54.opChamfer","BLEND_FACE",FACE,{"disambiguationData":[OSD([subQ2,subQ1,subQ0])]})]});}
            chamfer(context, id + "F56", {"entities" : qUnion([Q0, Q1]), "width" : 25.4 * mm, "tangentPropagation" : true});
        }
        {
            var Q0;
            {var subQ0=sQuery(id+"F51.wireOp",EDGE,"E68.top");var subQ1=sQuery(id+"F51.wireOp",EDGE,"E67.right");var subQ2=sQuery(id+"F51.wireOp",EDGE,"E67.bottom");var subQ3=makeQuery(id+"F52.opExtrude","SWEPT_FACE",FACE,{"disambiguationData":[OSD([subQ2,subQ0])]});Q0=makeQuery(id+"F56.opChamfer","BLEND_EDGE",EDGE,{"blendedFrom":[makeQuery(id+"F55.opChamfer","BLEND_EDGE",EDGE,{"blendedFrom":[makeQuery(id+"F54.opChamfer","BLEND_EDGE",EDGE,{"blendedFrom":[makeQuery(id+"F53.opChamfer","BLEND_EDGE",EDGE,{"blendedFrom":[makeQuery(id+"F52.opExtrude","SWEPT_EDGE",EDGE,{"disambiguationData":[OSD([subQ2,subQ1])]}),subQ3],"blendedInto":[subQ3]}),subQ3],"blendedInto":[subQ3]}),makeQuery(id+"F54.opChamfer","BLEND_FACE",FACE,{"disambiguationData":[OSD([subQ2,subQ1,subQ0])]})],"blendedInto":[makeQuery(id+"F54.opChamfer","BLEND_FACE",FACE,{"disambiguationData":[OSD([subQ2,subQ1,subQ0])]})]}),makeQuery(id+"F55.opChamfer","BLEND_FACE",FACE,{"disambiguationData":[OSD([subQ2,subQ1,subQ0])]})],"blendedInto":[makeQuery(id+"F55.opChamfer","BLEND_FACE",FACE,{"disambiguationData":[OSD([subQ2,subQ1,subQ0])]})]});}
            var Q1;
            {var subQ0=sQuery(id+"F51.wireOp",EDGE,"E68.right");var subQ1=sQuery(id+"F51.wireOp",EDGE,"E68.top");var subQ2=sQuery(id+"F51.wireOp",EDGE,"E67.bottom");var subQ3=makeQuery(id+"F52.opExtrude","SWEPT_FACE",FACE,{"disambiguationData":[OSD([subQ2,subQ1])]});Q1=makeQuery(id+"F56.opChamfer","BLEND_EDGE",EDGE,{"blendedFrom":[makeQuery(id+"F55.opChamfer","BLEND_EDGE",EDGE,{"blendedFrom":[makeQuery(id+"F54.opChamfer","BLEND_EDGE",EDGE,{"blendedFrom":[makeQuery(id+"F53.opChamfer","BLEND_EDGE",EDGE,{"blendedFrom":[makeQuery(id+"F52.opExtrude","SWEPT_EDGE",EDGE,{"disambiguationData":[OSD([subQ1,subQ0])]}),subQ3],"blendedInto":[subQ3]}),subQ3],"blendedInto":[subQ3]}),makeQuery(id+"F54.opChamfer","BLEND_FACE",FACE,{"disambiguationData":[OSD([subQ2,subQ1,subQ0])]})],"blendedInto":[makeQuery(id+"F54.opChamfer","BLEND_FACE",FACE,{"disambiguationData":[OSD([subQ2,subQ1,subQ0])]})]}),makeQuery(id+"F55.opChamfer","BLEND_FACE",FACE,{"disambiguationData":[OSD([subQ2,subQ1,subQ0])]})],"blendedInto":[makeQuery(id+"F55.opChamfer","BLEND_FACE",FACE,{"disambiguationData":[OSD([subQ2,subQ1,subQ0])]})]});}
            chamfer(context, id + "F57", {"entities" : qUnion([Q0, Q1]), "width" : 20.32 * mm, "tangentPropagation" : true});
        }
        {
            var Q0;
            {var subQ0=sQuery(id+"F51.wireOp",EDGE,"E68.top");var subQ1=sQuery(id+"F51.wireOp",EDGE,"E67.right");var subQ2=sQuery(id+"F51.wireOp",EDGE,"E67.bottom");var subQ3=makeQuery(id+"F52.opExtrude","SWEPT_FACE",FACE,{"disambiguationData":[OSD([subQ2,subQ0])]});Q0=makeQuery(id+"F57.opChamfer","BLEND_EDGE",EDGE,{"blendedFrom":[makeQuery(id+"F56.opChamfer","BLEND_EDGE",EDGE,{"blendedFrom":[makeQuery(id+"F55.opChamfer","BLEND_EDGE",EDGE,{"blendedFrom":[makeQuery(id+"F54.opChamfer","BLEND_EDGE",EDGE,{"blendedFrom":[makeQuery(id+"F53.opChamfer","BLEND_EDGE",EDGE,{"blendedFrom":[makeQuery(id+"F52.opExtrude","SWEPT_EDGE",EDGE,{"disambiguationData":[OSD([subQ2,subQ1])]}),subQ3],"blendedInto":[subQ3]}),subQ3],"blendedInto":[subQ3]}),makeQuery(id+"F54.opChamfer","BLEND_FACE",FACE,{"disambiguationData":[OSD([subQ2,subQ1,subQ0])]})],"blendedInto":[makeQuery(id+"F54.opChamfer","BLEND_FACE",FACE,{"disambiguationData":[OSD([subQ2,subQ1,subQ0])]})]}),makeQuery(id+"F55.opChamfer","BLEND_FACE",FACE,{"disambiguationData":[OSD([subQ2,subQ1,subQ0])]})],"blendedInto":[makeQuery(id+"F55.opChamfer","BLEND_FACE",FACE,{"disambiguationData":[OSD([subQ2,subQ1,subQ0])]})]}),makeQuery(id+"F52.opExtrude","CAP_FACE",FACE,{"disambiguationData":[OSD([subQ2,subQ1,subQ0,sQuery(id+"F51.wireOp",EDGE,"E68.right"),sQuery(id+"F51.wireOp",EDGE,"E69.top"),sQuery(id+"F51.wireOp",EDGE,"E69.right"),sQuery(id+"F51.wireOp",EDGE,"E70.top"),sQuery(id+"F51.wireOp",EDGE,"E70.right")])],"isStart":false})],"blendedInto":[makeQuery(id+"F52.opExtrude","CAP_FACE",FACE,{"disambiguationData":[OSD([subQ2,subQ1,subQ0,sQuery(id+"F51.wireOp",EDGE,"E68.right"),sQuery(id+"F51.wireOp",EDGE,"E69.top"),sQuery(id+"F51.wireOp",EDGE,"E69.right"),sQuery(id+"F51.wireOp",EDGE,"E70.top"),sQuery(id+"F51.wireOp",EDGE,"E70.right")])],"isStart":false})]});}
            var Q1;
            {var subQ0=sQuery(id+"F51.wireOp",EDGE,"E68.top");var subQ1=sQuery(id+"F51.wireOp",EDGE,"E67.right");var subQ2=sQuery(id+"F51.wireOp",EDGE,"E67.bottom");var subQ3=makeQuery(id+"F52.opExtrude","SWEPT_FACE",FACE,{"disambiguationData":[OSD([subQ2,subQ0])]});Q1=makeQuery(id+"F56.opChamfer","BLEND_EDGE",EDGE,{"blendedFrom":[makeQuery(id+"F55.opChamfer","BLEND_EDGE",EDGE,{"blendedFrom":[makeQuery(id+"F54.opChamfer","BLEND_EDGE",EDGE,{"blendedFrom":[makeQuery(id+"F53.opChamfer","BLEND_EDGE",EDGE,{"blendedFrom":[makeQuery(id+"F52.opExtrude","SWEPT_EDGE",EDGE,{"disambiguationData":[OSD([subQ2,subQ1])]}),subQ3],"blendedInto":[subQ3]}),subQ3],"blendedInto":[subQ3]}),makeQuery(id+"F54.opChamfer","BLEND_FACE",FACE,{"disambiguationData":[OSD([subQ2,subQ1,subQ0])]})],"blendedInto":[makeQuery(id+"F54.opChamfer","BLEND_FACE",FACE,{"disambiguationData":[OSD([subQ2,subQ1,subQ0])]})]}),makeQuery(id+"F52.opExtrude","CAP_FACE",FACE,{"disambiguationData":[OSD([subQ2,subQ1,subQ0,sQuery(id+"F51.wireOp",EDGE,"E68.right"),sQuery(id+"F51.wireOp",EDGE,"E69.top"),sQuery(id+"F51.wireOp",EDGE,"E69.right"),sQuery(id+"F51.wireOp",EDGE,"E70.top"),sQuery(id+"F51.wireOp",EDGE,"E70.right")])],"isStart":true})],"blendedInto":[makeQuery(id+"F52.opExtrude","CAP_FACE",FACE,{"disambiguationData":[OSD([subQ2,subQ1,subQ0,sQuery(id+"F51.wireOp",EDGE,"E68.right"),sQuery(id+"F51.wireOp",EDGE,"E69.top"),sQuery(id+"F51.wireOp",EDGE,"E69.right"),sQuery(id+"F51.wireOp",EDGE,"E70.top"),sQuery(id+"F51.wireOp",EDGE,"E70.right")])],"isStart":true})]});}
            var Q2;
            {var subQ0=sQuery(id+"F51.wireOp",EDGE,"E68.right");var subQ1=sQuery(id+"F51.wireOp",EDGE,"E68.top");var subQ2=sQuery(id+"F51.wireOp",EDGE,"E67.bottom");var subQ3=makeQuery(id+"F52.opExtrude","SWEPT_FACE",FACE,{"disambiguationData":[OSD([subQ2,subQ1])]});Q2=makeQuery(id+"F57.opChamfer","BLEND_EDGE",EDGE,{"blendedFrom":[makeQuery(id+"F56.opChamfer","BLEND_EDGE",EDGE,{"blendedFrom":[makeQuery(id+"F55.opChamfer","BLEND_EDGE",EDGE,{"blendedFrom":[makeQuery(id+"F54.opChamfer","BLEND_EDGE",EDGE,{"blendedFrom":[makeQuery(id+"F53.opChamfer","BLEND_EDGE",EDGE,{"blendedFrom":[makeQuery(id+"F52.opExtrude","SWEPT_EDGE",EDGE,{"disambiguationData":[OSD([subQ1,subQ0])]}),subQ3],"blendedInto":[subQ3]}),subQ3],"blendedInto":[subQ3]}),makeQuery(id+"F54.opChamfer","BLEND_FACE",FACE,{"disambiguationData":[OSD([subQ2,subQ1,subQ0])]})],"blendedInto":[makeQuery(id+"F54.opChamfer","BLEND_FACE",FACE,{"disambiguationData":[OSD([subQ2,subQ1,subQ0])]})]}),makeQuery(id+"F55.opChamfer","BLEND_FACE",FACE,{"disambiguationData":[OSD([subQ2,subQ1,subQ0])]})],"blendedInto":[makeQuery(id+"F55.opChamfer","BLEND_FACE",FACE,{"disambiguationData":[OSD([subQ2,subQ1,subQ0])]})]}),makeQuery(id+"F52.opExtrude","CAP_FACE",FACE,{"disambiguationData":[OSD([subQ2,sQuery(id+"F51.wireOp",EDGE,"E67.right"),subQ1,subQ0,sQuery(id+"F51.wireOp",EDGE,"E69.top"),sQuery(id+"F51.wireOp",EDGE,"E69.right"),sQuery(id+"F51.wireOp",EDGE,"E70.top"),sQuery(id+"F51.wireOp",EDGE,"E70.right")])],"isStart":true})],"blendedInto":[makeQuery(id+"F52.opExtrude","CAP_FACE",FACE,{"disambiguationData":[OSD([subQ2,sQuery(id+"F51.wireOp",EDGE,"E67.right"),subQ1,subQ0,sQuery(id+"F51.wireOp",EDGE,"E69.top"),sQuery(id+"F51.wireOp",EDGE,"E69.right"),sQuery(id+"F51.wireOp",EDGE,"E70.top"),sQuery(id+"F51.wireOp",EDGE,"E70.right")])],"isStart":true})]});}
            var Q3;
            {var subQ0=sQuery(id+"F51.wireOp",EDGE,"E68.right");var subQ1=sQuery(id+"F51.wireOp",EDGE,"E68.top");var subQ2=sQuery(id+"F51.wireOp",EDGE,"E67.bottom");var subQ3=makeQuery(id+"F52.opExtrude","SWEPT_FACE",FACE,{"disambiguationData":[OSD([subQ2,subQ1])]});Q3=makeQuery(id+"F57.opChamfer","BLEND_EDGE",EDGE,{"blendedFrom":[makeQuery(id+"F56.opChamfer","BLEND_EDGE",EDGE,{"blendedFrom":[makeQuery(id+"F55.opChamfer","BLEND_EDGE",EDGE,{"blendedFrom":[makeQuery(id+"F54.opChamfer","BLEND_EDGE",EDGE,{"blendedFrom":[makeQuery(id+"F53.opChamfer","BLEND_EDGE",EDGE,{"blendedFrom":[makeQuery(id+"F52.opExtrude","SWEPT_EDGE",EDGE,{"disambiguationData":[OSD([subQ1,subQ0])]}),subQ3],"blendedInto":[subQ3]}),subQ3],"blendedInto":[subQ3]}),makeQuery(id+"F54.opChamfer","BLEND_FACE",FACE,{"disambiguationData":[OSD([subQ2,subQ1,subQ0])]})],"blendedInto":[makeQuery(id+"F54.opChamfer","BLEND_FACE",FACE,{"disambiguationData":[OSD([subQ2,subQ1,subQ0])]})]}),makeQuery(id+"F55.opChamfer","BLEND_FACE",FACE,{"disambiguationData":[OSD([subQ2,subQ1,subQ0])]})],"blendedInto":[makeQuery(id+"F55.opChamfer","BLEND_FACE",FACE,{"disambiguationData":[OSD([subQ2,subQ1,subQ0])]})]}),makeQuery(id+"F52.opExtrude","CAP_FACE",FACE,{"disambiguationData":[OSD([subQ2,sQuery(id+"F51.wireOp",EDGE,"E67.right"),subQ1,subQ0,sQuery(id+"F51.wireOp",EDGE,"E69.top"),sQuery(id+"F51.wireOp",EDGE,"E69.right"),sQuery(id+"F51.wireOp",EDGE,"E70.top"),sQuery(id+"F51.wireOp",EDGE,"E70.right")])],"isStart":false})],"blendedInto":[makeQuery(id+"F52.opExtrude","CAP_FACE",FACE,{"disambiguationData":[OSD([subQ2,sQuery(id+"F51.wireOp",EDGE,"E67.right"),subQ1,subQ0,sQuery(id+"F51.wireOp",EDGE,"E69.top"),sQuery(id+"F51.wireOp",EDGE,"E69.right"),sQuery(id+"F51.wireOp",EDGE,"E70.top"),sQuery(id+"F51.wireOp",EDGE,"E70.right")])],"isStart":false})]});}
            var Q4;
            {var subQ0=sQuery(id+"F51.wireOp",EDGE,"E70.right");var subQ1=sQuery(id+"F51.wireOp",EDGE,"E70.top");var subQ2=sQuery(id+"F51.wireOp",EDGE,"E69.top");Q4=makeQuery(id+"F54.opChamfer","BLEND_EDGE",EDGE,{"blendedFrom":[makeQuery(id+"F53.opChamfer","BLEND_EDGE",EDGE,{"blendedFrom":[makeQuery(id+"F52.opExtrude","SWEPT_EDGE",EDGE,{"disambiguationData":[OSD([subQ1,subQ0])]}),makeQuery(id+"F52.opExtrude","SWEPT_FACE",FACE,{"disambiguationData":[OSD([subQ2,subQ1])]})],"blendedInto":[makeQuery(id+"F52.opExtrude","SWEPT_FACE",FACE,{"disambiguationData":[OSD([subQ2,subQ1])]})]}),makeQuery(id+"F52.opExtrude","CAP_FACE",FACE,{"disambiguationData":[OSD([sQuery(id+"F51.wireOp",EDGE,"E67.bottom"),sQuery(id+"F51.wireOp",EDGE,"E67.right"),sQuery(id+"F51.wireOp",EDGE,"E68.top"),sQuery(id+"F51.wireOp",EDGE,"E68.right"),subQ2,sQuery(id+"F51.wireOp",EDGE,"E69.right"),subQ1,subQ0])],"isStart":false})],"blendedInto":[makeQuery(id+"F52.opExtrude","CAP_FACE",FACE,{"disambiguationData":[OSD([sQuery(id+"F51.wireOp",EDGE,"E67.bottom"),sQuery(id+"F51.wireOp",EDGE,"E67.right"),sQuery(id+"F51.wireOp",EDGE,"E68.top"),sQuery(id+"F51.wireOp",EDGE,"E68.right"),subQ2,sQuery(id+"F51.wireOp",EDGE,"E69.right"),subQ1,subQ0])],"isStart":false})]});}
            var Q5;
            {var subQ0=sQuery(id+"F51.wireOp",EDGE,"E70.right");var subQ1=sQuery(id+"F51.wireOp",EDGE,"E70.top");var subQ2=sQuery(id+"F51.wireOp",EDGE,"E69.top");Q5=makeQuery(id+"F54.opChamfer","BLEND_EDGE",EDGE,{"blendedFrom":[makeQuery(id+"F53.opChamfer","BLEND_EDGE",EDGE,{"blendedFrom":[makeQuery(id+"F52.opExtrude","SWEPT_EDGE",EDGE,{"disambiguationData":[OSD([subQ1,subQ0])]}),makeQuery(id+"F52.opExtrude","SWEPT_FACE",FACE,{"disambiguationData":[OSD([subQ2,subQ1])]})],"blendedInto":[makeQuery(id+"F52.opExtrude","SWEPT_FACE",FACE,{"disambiguationData":[OSD([subQ2,subQ1])]})]}),makeQuery(id+"F52.opExtrude","CAP_FACE",FACE,{"disambiguationData":[OSD([sQuery(id+"F51.wireOp",EDGE,"E67.bottom"),sQuery(id+"F51.wireOp",EDGE,"E67.right"),sQuery(id+"F51.wireOp",EDGE,"E68.top"),sQuery(id+"F51.wireOp",EDGE,"E68.right"),subQ2,sQuery(id+"F51.wireOp",EDGE,"E69.right"),subQ1,subQ0])],"isStart":true})],"blendedInto":[makeQuery(id+"F52.opExtrude","CAP_FACE",FACE,{"disambiguationData":[OSD([sQuery(id+"F51.wireOp",EDGE,"E67.bottom"),sQuery(id+"F51.wireOp",EDGE,"E67.right"),sQuery(id+"F51.wireOp",EDGE,"E68.top"),sQuery(id+"F51.wireOp",EDGE,"E68.right"),subQ2,sQuery(id+"F51.wireOp",EDGE,"E69.right"),subQ1,subQ0])],"isStart":true})]});}
            var Q6;
            {var subQ0=sQuery(id+"F51.wireOp",EDGE,"E70.top");var subQ1=sQuery(id+"F51.wireOp",EDGE,"E69.right");var subQ2=sQuery(id+"F51.wireOp",EDGE,"E69.top");Q6=makeQuery(id+"F54.opChamfer","BLEND_EDGE",EDGE,{"blendedFrom":[makeQuery(id+"F53.opChamfer","BLEND_EDGE",EDGE,{"blendedFrom":[makeQuery(id+"F52.opExtrude","SWEPT_EDGE",EDGE,{"disambiguationData":[OSD([subQ2,subQ1])]}),makeQuery(id+"F52.opExtrude","SWEPT_FACE",FACE,{"disambiguationData":[OSD([subQ2,subQ0])]})],"blendedInto":[makeQuery(id+"F52.opExtrude","SWEPT_FACE",FACE,{"disambiguationData":[OSD([subQ2,subQ0])]})]}),makeQuery(id+"F52.opExtrude","CAP_FACE",FACE,{"disambiguationData":[OSD([sQuery(id+"F51.wireOp",EDGE,"E67.bottom"),sQuery(id+"F51.wireOp",EDGE,"E67.right"),sQuery(id+"F51.wireOp",EDGE,"E68.top"),sQuery(id+"F51.wireOp",EDGE,"E68.right"),subQ2,subQ1,subQ0,sQuery(id+"F51.wireOp",EDGE,"E70.right")])],"isStart":false})],"blendedInto":[makeQuery(id+"F52.opExtrude","CAP_FACE",FACE,{"disambiguationData":[OSD([sQuery(id+"F51.wireOp",EDGE,"E67.bottom"),sQuery(id+"F51.wireOp",EDGE,"E67.right"),sQuery(id+"F51.wireOp",EDGE,"E68.top"),sQuery(id+"F51.wireOp",EDGE,"E68.right"),subQ2,subQ1,subQ0,sQuery(id+"F51.wireOp",EDGE,"E70.right")])],"isStart":false})]});}
            var Q7;
            {var subQ0=sQuery(id+"F51.wireOp",EDGE,"E70.top");var subQ1=sQuery(id+"F51.wireOp",EDGE,"E69.right");var subQ2=sQuery(id+"F51.wireOp",EDGE,"E69.top");Q7=makeQuery(id+"F54.opChamfer","BLEND_EDGE",EDGE,{"blendedFrom":[makeQuery(id+"F53.opChamfer","BLEND_EDGE",EDGE,{"blendedFrom":[makeQuery(id+"F52.opExtrude","SWEPT_EDGE",EDGE,{"disambiguationData":[OSD([subQ2,subQ1])]}),makeQuery(id+"F52.opExtrude","SWEPT_FACE",FACE,{"disambiguationData":[OSD([subQ2,subQ0])]})],"blendedInto":[makeQuery(id+"F52.opExtrude","SWEPT_FACE",FACE,{"disambiguationData":[OSD([subQ2,subQ0])]})]}),makeQuery(id+"F52.opExtrude","CAP_FACE",FACE,{"disambiguationData":[OSD([sQuery(id+"F51.wireOp",EDGE,"E67.bottom"),sQuery(id+"F51.wireOp",EDGE,"E67.right"),sQuery(id+"F51.wireOp",EDGE,"E68.top"),sQuery(id+"F51.wireOp",EDGE,"E68.right"),subQ2,subQ1,subQ0,sQuery(id+"F51.wireOp",EDGE,"E70.right")])],"isStart":true})],"blendedInto":[makeQuery(id+"F52.opExtrude","CAP_FACE",FACE,{"disambiguationData":[OSD([sQuery(id+"F51.wireOp",EDGE,"E67.bottom"),sQuery(id+"F51.wireOp",EDGE,"E67.right"),sQuery(id+"F51.wireOp",EDGE,"E68.top"),sQuery(id+"F51.wireOp",EDGE,"E68.right"),subQ2,subQ1,subQ0,sQuery(id+"F51.wireOp",EDGE,"E70.right")])],"isStart":true})]});}
            chamfer(context, id + "F58", {"entities" : qUnion([Q0, Q1, Q2, Q3, Q4, Q5, Q6, Q7]), "width" : 6.35 * mm, "tangentPropagation" : true});
        }
        {
            var Q0;
            Q0=makeQuery(id+"F12.opExtrude","CAP_EDGE",EDGE,{"disambiguationData":[OSD([sQuery(id+"F11.wireOp",EDGE,"E7")])],"isStart":false});
            var Q1;
            Q1=makeQuery(id+"F14.opExtrude","CAP_EDGE",EDGE,{"disambiguationData":[OSD([sQuery(id+"F13.wireOp",EDGE,"E8")])],"isStart":false});
            var Q2;
            Q2=makeQuery(id+"F12.opExtrude","CAP_EDGE",EDGE,{"disambiguationData":[OSD([sQuery(id+"F11.wireOp",EDGE,"E7")])],"isStart":true});
            var Q3;
            Q3=makeQuery(id+"F14.opExtrude","CAP_EDGE",EDGE,{"disambiguationData":[OSD([sQuery(id+"F13.wireOp",EDGE,"E8")])],"isStart":true});
            chamfer(context, id + "F59", {"entities" : qUnion([Q0, Q1, Q2, Q3]), "width" : 5.08 * mm, "tangentPropagation" : true});
        }
        {
            var Q0;
            Q0=makeQuery(id+"F34.opExtrude","SWEPT_FACE",FACE,{"disambiguationData":[OSD([sQuery(id+"F33.wireOp",EDGE,"E59.bottom")])]});
            var sketch = newSketch(context, id + "F60", { "sketchPlane" : qUnion([Q0])});
            skLineSegment(sketch, "E71.bottom", {"start": v(-101.6, -171.45) * mm, "end": v(-114.3, -171.45) * mm});
            skLineSegment(sketch, "E71.top", {"start": v(-101.6, -179.07) * mm, "end": v(-114.3, -179.07) * mm});
            skLineSegment(sketch, "E71.left", {"start": v(-101.6, -171.45) * mm, "end": v(-101.6, -179.07) * mm});
            skLineSegment(sketch, "E71.right", {"start": v(-114.3, -171.45) * mm, "end": v(-114.3, -179.07) * mm});
            skSolve(sketch);
        }
        {
            var Q0;
            Q0 = qSketchRegion(id + "F60", true);
            extrude(context, id + "F61", {"entities" : qUnion([Q0]), "depth" : 12.7 * mm, "offsetDistance" : 25.4 * mm});
        }
        {
            var Q0;
            Q0=makeQuery(id+"F38.opExtrude","SWEPT_FACE",FACE,{"disambiguationData":[OSD([sQuery(id+"F29.wireOp",EDGE,"E51.top")])]});
            var sketch = newSketch(context, id + "F62", { "sketchPlane" : qUnion([Q0])});
            skLineSegment(sketch, "E72.bottom", {"start": v(-101.6, 179.07) * mm, "end": v(-114.3, 179.07) * mm});
            skLineSegment(sketch, "E72.top", {"start": v(-101.6, 171.45) * mm, "end": v(-114.3, 171.45) * mm});
            skLineSegment(sketch, "E72.left", {"start": v(-101.6, 179.07) * mm, "end": v(-101.6, 171.45) * mm});
            skLineSegment(sketch, "E72.right", {"start": v(-114.3, 179.07) * mm, "end": v(-114.3, 171.45) * mm});
            skSolve(sketch);
        }
        {
            var Q0;
            Q0 = qSketchRegion(id + "F62", true);
            extrude(context, id + "F63", {"entities" : qUnion([Q0]), "depth" : 12.7 * mm, "offsetDistance" : 25.4 * mm});
        }
        {
            var Q0;
            Q0=makeQuery(id+"F36.opExtrude","SWEPT_FACE",FACE,{"disambiguationData":[OSD([sQuery(id+"F31.wireOp",EDGE,"E55.top")])]});
            var sketch = newSketch(context, id + "F64", { "sketchPlane" : qUnion([Q0])});
            skLineSegment(sketch, "E73.bottom", {"start": v(101.59, -175.26) * mm, "end": v(114.3, -175.26) * mm});
            skLineSegment(sketch, "E73.top", {"start": v(101.59, -171.45) * mm, "end": v(114.3, -171.45) * mm});
            skLineSegment(sketch, "E73.left", {"start": v(114.3, -175.26) * mm, "end": v(114.3, -171.45) * mm});
            skLineSegment(sketch, "E73.right", {"start": v(101.59, -175.26) * mm, "end": v(101.59, -171.45) * mm});
            skLineSegment(sketch, "E74.bottom", {"start": v(101.6, -171.45) * mm, "end": v(114.3, -171.45) * mm});
            skLineSegment(sketch, "E74.top", {"start": v(101.6, -179.07) * mm, "end": v(114.3, -179.07) * mm});
            skLineSegment(sketch, "E74.left", {"start": v(101.6, -171.45) * mm, "end": v(101.6, -179.07) * mm});
            skLineSegment(sketch, "E74.right", {"start": v(114.3, -171.45) * mm, "end": v(114.3, -179.07) * mm});
            skSolve(sketch);
        }
        {
            var Q0;
            Q0 = qSketchRegion(id + "F64", true);
            extrude(context, id + "F65", {"entities" : qUnion([Q0]), "depth" : 12.7 * mm, "offsetDistance" : 25.4 * mm});
        }
        {
            var Q0;
            Q0=makeQuery(id+"F35.opExtrude","SWEPT_FACE",FACE,{"disambiguationData":[OSD([sQuery(id+"F32.wireOp",EDGE,"E57.top")])]});
            var sketch = newSketch(context, id + "F66", { "sketchPlane" : qUnion([Q0])});
            skLineSegment(sketch, "E75.bottom", {"start": v(-114.3, 175.26) * mm, "end": v(-101.6, 175.26) * mm});
            skLineSegment(sketch, "E75.top", {"start": v(-114.3, 171.45) * mm, "end": v(-101.6, 171.45) * mm});
            skLineSegment(sketch, "E75.left", {"start": v(-114.3, 171.45) * mm, "end": v(-114.3, 175.26) * mm});
            skLineSegment(sketch, "E75.right", {"start": v(-101.6, 171.45) * mm, "end": v(-101.6, 175.26) * mm});
            skLineSegment(sketch, "E76.top", {"start": v(-114.3, 179.07) * mm, "end": v(-101.6, 179.07) * mm});
            skLineSegment(sketch, "E76.left", {"start": v(-114.3, 171.45) * mm, "end": v(-114.3, 179.07) * mm});
            skLineSegment(sketch, "E76.right", {"start": v(-101.6, 171.45) * mm, "end": v(-101.6, 179.07) * mm});
            skSolve(sketch);
        }
        {
            var Q0;
            Q0 = qSketchRegion(id + "F66", true);
            extrude(context, id + "F67", {"entities" : qUnion([Q0]), "depth" : 12.7 * mm, "offsetDistance" : 25.4 * mm});
        }
        {
            var Q0;
            Q0=makeQuery(id+"F35.opExtrude","SWEPT_FACE",FACE,{"disambiguationData":[OSD([sQuery(id+"F32.wireOp",EDGE,"E57.bottom")])]});
            var sketch = newSketch(context, id + "F68", { "sketchPlane" : qUnion([Q0])});
            skLineSegment(sketch, "E77.bottom", {"start": v(-114.3, -179.07) * mm, "end": v(-101.6, -179.07) * mm});
            skLineSegment(sketch, "E77.top", {"start": v(-114.3, -171.45) * mm, "end": v(-101.6, -171.45) * mm});
            skLineSegment(sketch, "E77.left", {"start": v(-114.3, -179.07) * mm, "end": v(-114.3, -171.45) * mm});
            skLineSegment(sketch, "E77.right", {"start": v(-101.6, -179.07) * mm, "end": v(-101.6, -171.45) * mm});
            skSolve(sketch);
        }
        {
            var Q0;
            Q0 = qSketchRegion(id + "F68", true);
            extrude(context, id + "F69", {"entities" : qUnion([Q0]), "depth" : 12.7 * mm, "offsetDistance" : 25.4 * mm});
        }
        {
            var Q0;
            Q0=makeQuery(id+"F39.opExtrude","SWEPT_FACE",FACE,{"disambiguationData":[OSD([sQuery(id+"F28.wireOp",EDGE,"E50.top")])]});
            var sketch = newSketch(context, id + "F70", { "sketchPlane" : qUnion([Q0])});
            skLineSegment(sketch, "E78.bottom", {"start": v(101.63, 179.07) * mm, "end": v(114.3, 179.07) * mm});
            skLineSegment(sketch, "E78.top", {"start": v(101.63, 171.45) * mm, "end": v(114.3, 171.45) * mm});
            skLineSegment(sketch, "E78.left", {"start": v(101.63, 179.07) * mm, "end": v(101.63, 171.45) * mm});
            skLineSegment(sketch, "E78.right", {"start": v(114.3, 179.07) * mm, "end": v(114.3, 171.45) * mm});
            skSolve(sketch);
        }
        {
            var Q0;
            Q0 = qSketchRegion(id + "F70", true);
            extrude(context, id + "F71", {"entities" : qUnion([Q0]), "depth" : 12.7 * mm, "offsetDistance" : 25.4 * mm});
        }
        {
            var Q0;
            Q0=makeQuery(id+"F38.opExtrude","SWEPT_FACE",FACE,{"disambiguationData":[OSD([sQuery(id+"F29.wireOp",EDGE,"E52.top")])]});
            var sketch = newSketch(context, id + "F72", { "sketchPlane" : qUnion([Q0])});
            skLineSegment(sketch, "E79.bottom", {"start": v(101.59, 179.07) * mm, "end": v(114.27, 179.07) * mm});
            skLineSegment(sketch, "E79.top", {"start": v(101.59, 171.45) * mm, "end": v(114.27, 171.45) * mm});
            skLineSegment(sketch, "E79.left", {"start": v(101.59, 179.07) * mm, "end": v(101.59, 171.45) * mm});
            skLineSegment(sketch, "E79.right", {"start": v(114.27, 179.07) * mm, "end": v(114.27, 171.45) * mm});
            skSolve(sketch);
        }
        {
            var Q0;
            Q0 = qSketchRegion(id + "F72", true);
            extrude(context, id + "F73", {"entities" : qUnion([Q0]), "depth" : 12.7 * mm, "offsetDistance" : 25.4 * mm});
        }
        {
            var Q0;
            Q0=makeQuery(id+"F37.opExtrude","SWEPT_FACE",FACE,{"disambiguationData":[OSD([sQuery(id+"F30.wireOp",EDGE,"E53.top")])]});
            var sketch = newSketch(context, id + "F74", { "sketchPlane" : qUnion([Q0])});
            skLineSegment(sketch, "E80.bottom", {"start": v(114.3, -171.45) * mm, "end": v(101.6, -171.45) * mm});
            skLineSegment(sketch, "E80.top", {"start": v(114.3, -179.07) * mm, "end": v(101.6, -179.07) * mm});
            skLineSegment(sketch, "E80.left", {"start": v(114.3, -171.45) * mm, "end": v(114.3, -179.07) * mm});
            skLineSegment(sketch, "E80.right", {"start": v(101.6, -171.45) * mm, "end": v(101.6, -179.07) * mm});
            skSolve(sketch);
        }
        {
            var Q0;
            Q0 = qSketchRegion(id + "F74", true);
            extrude(context, id + "F75", {"entities" : qUnion([Q0]), "depth" : 12.7 * mm, "offsetDistance" : 25.4 * mm});
        }
        {
            var Q0;
            Q0=makeQuery(id+"F35.opExtrude","SWEPT_FACE",FACE,{"disambiguationData":[OSD([sQuery(id+"F32.wireOp",EDGE,"E58.top")])]});
            var sketch = newSketch(context, id + "F76", { "sketchPlane" : qUnion([Q0])});
            skLineSegment(sketch, "E81.bottom", {"start": v(114.3, 171.45) * mm, "end": v(101.6, 171.45) * mm});
            skLineSegment(sketch, "E81.top", {"start": v(114.3, 179.07) * mm, "end": v(101.6, 179.07) * mm});
            skLineSegment(sketch, "E81.left", {"start": v(114.3, 171.45) * mm, "end": v(114.3, 179.07) * mm});
            skLineSegment(sketch, "E81.right", {"start": v(101.6, 171.45) * mm, "end": v(101.6, 179.07) * mm});
            skSolve(sketch);
        }
        {
            var Q0;
            Q0 = qSketchRegion(id + "F76", true);
            extrude(context, id + "F77", {"entities" : qUnion([Q0]), "depth" : 12.7 * mm, "offsetDistance" : 25.4 * mm});
        }
        {
            var Q0;
            Q0=makeQuery(id+"F35.opExtrude","SWEPT_FACE",FACE,{"disambiguationData":[OSD([sQuery(id+"F32.wireOp",EDGE,"E58.bottom")])]});
            var sketch = newSketch(context, id + "F78", { "sketchPlane" : qUnion([Q0])});
            skLineSegment(sketch, "E82.bottom", {"start": v(114.37, -175.26) * mm, "end": v(101.61, -175.26) * mm});
            skLineSegment(sketch, "E82.top", {"start": v(114.37, -171.45) * mm, "end": v(101.61, -171.45) * mm});
            skLineSegment(sketch, "E82.left", {"start": v(114.37, -171.45) * mm, "end": v(114.37, -175.26) * mm});
            skLineSegment(sketch, "E82.right", {"start": v(101.61, -171.45) * mm, "end": v(101.61, -175.26) * mm});
            skLineSegment(sketch, "E83.bottom", {"start": v(101.6, -179.07) * mm, "end": v(114.37, -179.07) * mm});
            skLineSegment(sketch, "E83.top", {"start": v(101.6, -171.45) * mm, "end": v(114.37, -171.45) * mm});
            skLineSegment(sketch, "E83.left", {"start": v(101.6, -179.07) * mm, "end": v(101.6, -171.45) * mm});
            skLineSegment(sketch, "E83.right", {"start": v(114.37, -179.07) * mm, "end": v(114.37, -171.45) * mm});
            skSolve(sketch);
        }
        {
            var Q0;
            Q0 = qSketchRegion(id + "F78", true);
            extrude(context, id + "F79", {"entities" : qUnion([Q0]), "depth" : 12.7 * mm, "offsetDistance" : 25.4 * mm});
        }
        {
            var Q0;
            Q0=makeQuery(id+"F71.opExtrude","SWEPT_FACE",FACE,{"disambiguationData":[OSD([sQuery(id+"F70.wireOp",EDGE,"E78.right")])]});
            var sketch = newSketch(context, id + "F80", { "sketchPlane" : qUnion([Q0])});
            skLineSegment(sketch, "E84", {"start": v(-107.79, 171.45) * mm, "end": v(-103.27, 179.27) * mm});
            skLineSegment(sketch, "E85", {"start": v(-103.27, 179.27) * mm, "end": v(-117.55, 181.53) * mm});
            skLineSegment(sketch, "E86", {"start": v(-117.55, 181.53) * mm, "end": v(-115.04, 170.3) * mm});
            skLineSegment(sketch, "E87", {"start": v(-115.04, 170.3) * mm, "end": v(-107.79, 171.45) * mm});
            skSolve(sketch);
        }
        {
            var Q0;
            Q0 = qSketchRegion(id + "F80", true);
            extrude(context, id + "F81", {"entities" : qUnion([Q0]), "operationType" : NewBodyOperationType.REMOVE, "oppositeDirection" : true, "depth" : 25.4 * mm, "offsetDistance" : 25.4 * mm});
        }
        {
            var Q0;
            Q0=makeQuery(id+"F73.opExtrude","SWEPT_FACE",FACE,{"disambiguationData":[OSD([sQuery(id+"F72.wireOp",EDGE,"E79.right")])]});
            var sketch = newSketch(context, id + "F82", { "sketchPlane" : qUnion([Q0])});
            skLineSegment(sketch, "E88", {"start": v(94.59, 179.07) * mm, "end": v(107.55, 179.07) * mm});
            skLineSegment(sketch, "E89", {"start": v(107.55, 179.07) * mm, "end": v(99.24, 188.92) * mm});
            skLineSegment(sketch, "E90", {"start": v(99.24, 188.92) * mm, "end": v(89.27, 184.77) * mm});
            skLineSegment(sketch, "E91", {"start": v(89.27, 184.77) * mm, "end": v(94.59, 179.07) * mm});
            skSolve(sketch);
        }
        {
            var Q0;
            Q0 = qSketchRegion(id + "F82", true);
            extrude(context, id + "F83", {"entities" : qUnion([Q0]), "operationType" : NewBodyOperationType.REMOVE, "oppositeDirection" : true, "depth" : 25.4 * mm, "offsetDistance" : 25.4 * mm});
        }
        {
            var Q0;
            Q0=makeQuery(id+"F63.opExtrude","SWEPT_FACE",FACE,{"disambiguationData":[OSD([sQuery(id+"F62.wireOp",EDGE,"E72.right")])]});
            var sketch = newSketch(context, id + "F84", { "sketchPlane" : qUnion([Q0])});
            skLineSegment(sketch, "E92", {"start": v(-94.59, 179.07) * mm, "end": v(-105.29, 179.07) * mm});
            skLineSegment(sketch, "E93", {"start": v(-105.29, 179.07) * mm, "end": v(-102.17, 186.26) * mm});
            skLineSegment(sketch, "E94", {"start": v(-102.17, 186.26) * mm, "end": v(-96.88, 186.88) * mm});
            skLineSegment(sketch, "E95", {"start": v(-96.88, 186.88) * mm, "end": v(-87.4, 183.66) * mm});
            skLineSegment(sketch, "E96", {"start": v(-87.4, 183.66) * mm, "end": v(-90.79, 180.55) * mm});
            skLineSegment(sketch, "E97", {"start": v(-90.79, 180.55) * mm, "end": v(-94.59, 179.07) * mm});
            skSolve(sketch);
        }
        {
            var Q0;
            Q0 = qSketchRegion(id + "F84", true);
            extrude(context, id + "F85", {"entities" : qUnion([Q0]), "operationType" : NewBodyOperationType.REMOVE, "oppositeDirection" : true, "depth" : 25.4 * mm, "offsetDistance" : 25.4 * mm});
        }
        {
            var Q0;
            Q0=makeQuery(id+"F61.opExtrude","SWEPT_FACE",FACE,{"disambiguationData":[OSD([sQuery(id+"F60.wireOp",EDGE,"E71.right")])]});
            var sketch = newSketch(context, id + "F86", { "sketchPlane" : qUnion([Q0])});
            skLineSegment(sketch, "E98", {"start": v(94.59, 179.07) * mm, "end": v(112.65, 179.07) * mm});
            skLineSegment(sketch, "E99", {"start": v(112.65, 179.07) * mm, "end": v(103.07, 190.54) * mm});
            skLineSegment(sketch, "E100", {"start": v(103.07, 190.54) * mm, "end": v(88.8, 190.54) * mm});
            skLineSegment(sketch, "E101", {"start": v(88.8, 190.54) * mm, "end": v(89.94, 183.3) * mm});
            skLineSegment(sketch, "E102", {"start": v(89.94, 183.3) * mm, "end": v(94.59, 179.07) * mm});
            skSolve(sketch);
        }
        {
            var Q0;
            Q0 = qSketchRegion(id + "F86", true);
            extrude(context, id + "F87", {"entities" : qUnion([Q0]), "operationType" : NewBodyOperationType.REMOVE, "oppositeDirection" : true, "depth" : 25.4 * mm, "offsetDistance" : 25.4 * mm});
        }
        {
            var Q0;
            Q0=makeQuery(id+"F69.opExtrude","SWEPT_FACE",FACE,{"disambiguationData":[OSD([sQuery(id+"F68.wireOp",EDGE,"E77.left")])]});
            var sketch = newSketch(context, id + "F88", { "sketchPlane" : qUnion([Q0])});
            skLineSegment(sketch, "E103", {"start": v(202.37, 7.62) * mm, "end": v(207.53, -1.3) * mm});
            skLineSegment(sketch, "E104", {"start": v(207.53, -1.3) * mm, "end": v(219.65, 16.33) * mm});
            skLineSegment(sketch, "E105", {"start": v(219.65, 16.33) * mm, "end": v(202.64, 16.33) * mm});
            skLineSegment(sketch, "E106", {"start": v(202.64, 16.33) * mm, "end": v(202.37, 7.62) * mm});
            skSolve(sketch);
        }
        {
            var Q0;
            Q0 = qSketchRegion(id + "F88", true);
            extrude(context, id + "F89", {"entities" : qUnion([Q0]), "operationType" : NewBodyOperationType.REMOVE, "oppositeDirection" : true, "depth" : 252.48 * mm, "offsetDistance" : 25.4 * mm});
        }
        {
            var Q0;
            Q0=makeQuery(id+"F67.opExtrude","SWEPT_FACE",FACE,{"disambiguationData":[OSD([sQuery(id+"F66.wireOp",EDGE,"E76.left")])]});
            var sketch = newSketch(context, id + "F90", { "sketchPlane" : qUnion([Q0])});
            skLineSegment(sketch, "E107", {"start": v(94.59, -179.07) * mm, "end": v(108.24, -179.07) * mm});
            skLineSegment(sketch, "E108", {"start": v(108.24, -179.07) * mm, "end": v(105.59, -192.45) * mm});
            skLineSegment(sketch, "E109", {"start": v(105.59, -192.45) * mm, "end": v(83.28, -186.26) * mm});
            skLineSegment(sketch, "E110", {"start": v(83.28, -186.26) * mm, "end": v(94.59, -179.07) * mm});
            skSolve(sketch);
        }
        {
            var Q0;
            Q0 = qSketchRegion(id + "F90", true);
            extrude(context, id + "F91", {"entities" : qUnion([Q0]), "operationType" : NewBodyOperationType.REMOVE, "oppositeDirection" : true, "depth" : 25.4 * mm, "offsetDistance" : 25.4 * mm});
        }
        {
            var Q0;
            Q0=makeQuery(id+"F65.opExtrude","SWEPT_FACE",FACE,{"disambiguationData":[OSD([sQuery(id+"F64.wireOp",EDGE,"E73.left")])]});
            var sketch = newSketch(context, id + "F92", { "sketchPlane" : qUnion([Q0])});
            skLineSegment(sketch, "E111", {"start": v(-107.79, -171.45) * mm, "end": v(-101.43, -182.45) * mm});
            skLineSegment(sketch, "E112", {"start": v(-101.43, -182.45) * mm, "end": v(-116.72, -179.17) * mm});
            skLineSegment(sketch, "E113", {"start": v(-116.72, -179.17) * mm, "end": v(-116.72, -166.43) * mm});
            skLineSegment(sketch, "E114", {"start": v(-116.72, -166.43) * mm, "end": v(-107.79, -171.45) * mm});
            skSolve(sketch);
        }
        {
            var Q0;
            Q0 = qSketchRegion(id + "F92", true);
            extrude(context, id + "F93", {"entities" : qUnion([Q0]), "operationType" : NewBodyOperationType.REMOVE, "oppositeDirection" : true, "depth" : 259.33 * mm, "offsetDistance" : 25.4 * mm});
        }
        {
            var Q0;
            Q0 = qSketchRegion(id + "F78", true);
            extrude(context, id + "F94", {"entities" : qUnion([Q0]), "depth" : 12.7 * mm, "offsetDistance" : 25.4 * mm});
        }
        {
            var Q0;
            Q0=makeQuery(id+"F79.opExtrude","SWEPT_FACE",FACE,{"disambiguationData":[OSD([sQuery(id+"F78.wireOp",EDGE,"E83.right")])]});
            var sketch = newSketch(context, id + "F95", { "sketchPlane" : qUnion([Q0])});
            skLineSegment(sketch, "E115", {"start": v(-202.37, 7.62) * mm, "end": v(-207.38, -0.89) * mm});
            skLineSegment(sketch, "E116", {"start": v(-207.38, -0.89) * mm, "end": v(-211.86, 8.17) * mm});
            skLineSegment(sketch, "E117", {"start": v(-211.86, 8.17) * mm, "end": v(-208.96, 9.82) * mm});
            skLineSegment(sketch, "E118", {"start": v(-208.96, 9.82) * mm, "end": v(-205.77, 11.66) * mm});
            skLineSegment(sketch, "E119", {"start": v(-205.77, 11.66) * mm, "end": v(-202.04, 11.66) * mm});
            skLineSegment(sketch, "E120", {"start": v(-202.04, 11.66) * mm, "end": v(-202.37, 7.62) * mm});
            skSolve(sketch);
        }
        {
            var Q0;
            Q0 = qSketchRegion(id + "F95", true);
            extrude(context, id + "F96", {"entities" : qUnion([Q0]), "operationType" : NewBodyOperationType.REMOVE, "oppositeDirection" : true, "depth" : 25.4 * mm, "offsetDistance" : 25.4 * mm});
        }
        {
            var Q0;
            Q0=makeQuery(id+"F38.opExtrude","SWEPT_FACE",FACE,{"disambiguationData":[OSD([sQuery(id+"F29.wireOp",EDGE,"E52.bottom")])]});
            var sketch = newSketch(context, id + "F97", { "sketchPlane" : qUnion([Q0])});
            skLineSegment(sketch, "E121.bottom", {"start": v(114.27, -179.07) * mm, "end": v(101.59, -179.07) * mm});
            skLineSegment(sketch, "E121.top", {"start": v(114.27, -171.45) * mm, "end": v(101.59, -171.45) * mm});
            skLineSegment(sketch, "E121.left", {"start": v(114.27, -179.07) * mm, "end": v(114.27, -171.45) * mm});
            skLineSegment(sketch, "E121.right", {"start": v(101.59, -179.07) * mm, "end": v(101.59, -171.45) * mm});
            skSolve(sketch);
        }
        {
            var Q0;
            Q0 = qSketchRegion(id + "F97", true);
            extrude(context, id + "F98", {"entities" : qUnion([Q0]), "depth" : 12.7 * mm, "offsetDistance" : 25.4 * mm});
        }
        {
            var Q0;
            Q0=makeQuery(id+"F98.opExtrude","SWEPT_FACE",FACE,{"disambiguationData":[OSD([sQuery(id+"F97.wireOp",EDGE,"E121.left")])]});
            var sketch = newSketch(context, id + "F99", { "sketchPlane" : qUnion([Q0])});
            skLineSegment(sketch, "E122", {"start": v(202.37, -7.62) * mm, "end": v(208.63, 3.2) * mm});
            skLineSegment(sketch, "E123", {"start": v(208.63, 3.2) * mm, "end": v(218.78, -11) * mm});
            skLineSegment(sketch, "E124", {"start": v(218.78, -11) * mm, "end": v(203.57, -17.06) * mm});
            skLineSegment(sketch, "E125", {"start": v(203.57, -17.06) * mm, "end": v(202.37, -7.62) * mm});
            skSolve(sketch);
        }
        {
            var Q0;
            Q0 = qSketchRegion(id + "F99", true);
            extrude(context, id + "F100", {"entities" : qUnion([Q0]), "operationType" : NewBodyOperationType.REMOVE, "oppositeDirection" : true, "depth" : 25.4 * mm, "offsetDistance" : 25.4 * mm});
        }
        {
            var Q0;
            Q0=makeQuery(id+"F37.opExtrude","SWEPT_FACE",FACE,{"disambiguationData":[OSD([sQuery(id+"F30.wireOp",EDGE,"E54.bottom")])]});
            var sketch = newSketch(context, id + "F101", { "sketchPlane" : qUnion([Q0])});
            skLineSegment(sketch, "E126.bottom", {"start": v(-101.59, 171.45) * mm, "end": v(-114.3, 171.45) * mm});
            skLineSegment(sketch, "E126.top", {"start": v(-101.59, 179.07) * mm, "end": v(-114.3, 179.07) * mm});
            skLineSegment(sketch, "E126.left", {"start": v(-101.59, 171.45) * mm, "end": v(-101.59, 179.07) * mm});
            skLineSegment(sketch, "E126.right", {"start": v(-114.3, 171.45) * mm, "end": v(-114.3, 179.07) * mm});
            skSolve(sketch);
        }
        {
            var Q0;
            Q0 = qSketchRegion(id + "F101", true);
            extrude(context, id + "F102", {"entities" : qUnion([Q0]), "depth" : 12.7 * mm, "offsetDistance" : 25.4 * mm});
        }
        {
            var Q0;
            Q0=makeQuery(id+"F102.opExtrude","SWEPT_FACE",FACE,{"disambiguationData":[OSD([sQuery(id+"F101.wireOp",EDGE,"E126.right")])]});
            var sketch = newSketch(context, id + "F103", { "sketchPlane" : qUnion([Q0])});
            skLineSegment(sketch, "E127", {"start": v(-199, 13.48) * mm, "end": v(-207.75, -1.5) * mm});
            skPoint(sketch, "E127.endSnap0", {"position": v(-207.75, 1.69) * mm});
            skLineSegment(sketch, "E128", {"start": v(-207.75, -1.5) * mm, "end": v(-212.99, 8.53) * mm});
            skLineSegment(sketch, "E129", {"start": v(-212.99, 8.53) * mm, "end": v(-199, 13.48) * mm});
            skSolve(sketch);
        }
        {
            var Q0;
            Q0 = qSketchRegion(id + "F103", true);
            extrude(context, id + "F104", {"entities" : qUnion([Q0]), "operationType" : NewBodyOperationType.REMOVE, "oppositeDirection" : true, "depth" : 25.4 * mm, "offsetDistance" : 25.4 * mm});
        }
        {
            var Q0;
            Q0=makeQuery(id+"F77.opExtrude","SWEPT_FACE",FACE,{"disambiguationData":[OSD([sQuery(id+"F76.wireOp",EDGE,"E81.left")])]});
            var sketch = newSketch(context, id + "F105", { "sketchPlane" : qUnion([Q0])});
            skLineSegment(sketch, "E130", {"start": v(-87.48, -179.07) * mm, "end": v(-106.14, -179.07) * mm});
            skLineSegment(sketch, "E131", {"start": v(-106.14, -179.07) * mm, "end": v(-105.59, -188.47) * mm});
            skLineSegment(sketch, "E132", {"start": v(-105.59, -188.47) * mm, "end": v(-89.14, -188.98) * mm});
            skLineSegment(sketch, "E133", {"start": v(-89.14, -188.98) * mm, "end": v(-87.48, -179.07) * mm});
            skSolve(sketch);
        }
        {
            var Q0;
            Q0 = qSketchRegion(id + "F105", true);
            extrude(context, id + "F106", {"entities" : qUnion([Q0]), "operationType" : NewBodyOperationType.REMOVE, "oppositeDirection" : true, "depth" : 25.4 * mm, "offsetDistance" : 25.4 * mm});
        }
        {
            var Q0;
            Q0=makeQuery(id+"F75.opExtrude","SWEPT_FACE",FACE,{"disambiguationData":[OSD([sQuery(id+"F74.wireOp",EDGE,"E80.left")])]});
            var sketch = newSketch(context, id + "F107", { "sketchPlane" : qUnion([Q0])});
            skLineSegment(sketch, "E134", {"start": v(90.77, -179.07) * mm, "end": v(107.22, -179.07) * mm});
            skLineSegment(sketch, "E135", {"start": v(107.22, -179.07) * mm, "end": v(98.97, -187.42) * mm});
            skLineSegment(sketch, "E136", {"start": v(98.97, -187.42) * mm, "end": v(86.75, -185.13) * mm});
            skLineSegment(sketch, "E137", {"start": v(86.75, -185.13) * mm, "end": v(90.77, -179.07) * mm});
            skSolve(sketch);
        }
        {
            var Q0;
            Q0 = qSketchRegion(id + "F107", true);
            extrude(context, id + "F108", {"entities" : qUnion([Q0]), "operationType" : NewBodyOperationType.REMOVE, "oppositeDirection" : true, "depth" : 25.4 * mm, "offsetDistance" : 25.4 * mm});
        }
        {
            var Q0;
            Q0=qCreatedBy(makeId("Top.planeOp"),FACE);
            cPlane(context, id + "F109", {"entities" : qUnion([Q0]), "cplaneType" : CPlaneType.OFFSET, "offset" : 58.42 * mm, "oppositeDirection" : true, "width" : 152.4 * mm, "height" : 152.4 * mm});
        }
        {
            var Q0;
            Q0=qCreatedBy(id+"F109.planeOp",FACE);
            var sketch = newSketch(context, id + "F110", { "sketchPlane" : qUnion([Q0])});
            skLineSegment(sketch, "E138.bottom", {"start": v(14.3, -12.32) * mm, "end": v(-14.3, -12.32) * mm});
            skLineSegment(sketch, "E138.top", {"start": v(14.3, 12.32) * mm, "end": v(-14.3, 12.32) * mm});
            skLineSegment(sketch, "E138.left", {"start": v(14.3, -12.32) * mm, "end": v(14.3, 12.32) * mm});
            skLineSegment(sketch, "E138.right", {"start": v(-14.3, -12.32) * mm, "end": v(-14.3, 12.32) * mm});
            skPoint(sketch, "E138.middle", {"position": v(0, 0) * mm});
            skSolve(sketch);
        }
        {
            var Q0;
            Q0 = qSketchRegion(id + "F110", true);
            extrude(context, id + "F111", {"entities" : qUnion([Q0]), "depth" : 11.43 * mm, "offsetDistance" : 25.4 * mm});
        }
        {
            var Q0;
            Q0=qCreatedBy(makeId("Top.planeOp"),FACE);
            cPlane(context, id + "F112", {"entities" : qUnion([Q0]), "cplaneType" : CPlaneType.OFFSET, "offset" : 33.53 * mm, "width" : 152.4 * mm, "height" : 152.4 * mm});
        }
        {
            var Q0;
            Q0=qCreatedBy(id+"F112.planeOp",FACE);
            var sketch = newSketch(context, id + "F113", { "sketchPlane" : qUnion([Q0])});
            skLineSegment(sketch, "E139.bottom", {"start": v(-61.57, 1.58) * mm, "end": v(-42.73, 1.58) * mm});
            skLineSegment(sketch, "E139.top", {"start": v(-61.57, -1.6) * mm, "end": v(-42.73, -1.6) * mm});
            skLineSegment(sketch, "E139.left", {"start": v(-61.57, 1.58) * mm, "end": v(-61.57, -1.6) * mm});
            skLineSegment(sketch, "E139.right", {"start": v(-42.73, 1.58) * mm, "end": v(-42.73, -1.6) * mm});
            skSolve(sketch);
        }
        {
            var Q0;
            Q0 = qSketchRegion(id + "F113", true);
            extrude(context, id + "F114", {"entities" : qUnion([Q0]), "operationType" : NewBodyOperationType.ADD, "depth" : 6.35 * mm, "offsetDistance" : 25.4 * mm});
        }
        {
            var Q0;
            Q0=makeQuery(id+"F114.opExtrude","CAP_FACE",FACE,{"disambiguationData":[OSD([sQuery(id+"F113.wireOp",EDGE,"E139.bottom"),sQuery(id+"F113.wireOp",EDGE,"E139.top"),sQuery(id+"F113.wireOp",EDGE,"E139.left"),sQuery(id+"F113.wireOp",EDGE,"E139.right")])],"isStart":false});
            var sketch = newSketch(context, id + "F115", { "sketchPlane" : qUnion([Q0])});
            skCircle(sketch, "E140", {"center": v(-59.03, -0.01) * mm, "radius": 0.95 * mm});
            skPoint(sketch, "E140.centerSnap0", {"position": v(-61.57, -0.01) * mm});
            skCircle(sketch, "E141", {"center": v(-52.13, 0) * mm, "radius": 0.95 * mm});
            skCircle(sketch, "E142", {"center": v(-45.27, -0.01) * mm, "radius": 0.95 * mm});
            skPoint(sketch, "E142.centerSnap0", {"position": v(-42.73, -0.01) * mm});
            skSolve(sketch);
        }
        {
            var Q0;
            Q0 = qSketchRegion(id + "F115", true);
            extrude(context, id + "F116", {"entities" : qUnion([Q0]), "operationType" : NewBodyOperationType.ADD, "depth" : 5.08 * mm, "offsetDistance" : 25.4 * mm});
        }
        {
            var Q0;
            Q0=makeQuery(id+"F116.opExtrude","CAP_FACE",FACE,{"disambiguationData":[OSD([sQuery(id+"F115.wireOp",EDGE,"E141")])],"isStart":false});
            var sketch = newSketch(context, id + "F117", { "sketchPlane" : qUnion([Q0])});
            skLineSegment(sketch, "E143.bottom", {"start": v(-61.57, 1.58) * mm, "end": v(-42.73, 1.58) * mm});
            skLineSegment(sketch, "E143.top", {"start": v(-61.57, -1.6) * mm, "end": v(-42.73, -1.6) * mm});
            skLineSegment(sketch, "E143.left", {"start": v(-61.57, 1.58) * mm, "end": v(-61.57, -1.6) * mm});
            skLineSegment(sketch, "E143.right", {"start": v(-42.73, 1.58) * mm, "end": v(-42.73, -1.6) * mm});
            skSolve(sketch);
        }
        {
            var Q0;
            Q0 = qSketchRegion(id + "F117", true);
            extrude(context, id + "F118", {"entities" : qUnion([Q0]), "operationType" : NewBodyOperationType.ADD, "depth" : 6.35 * mm, "offsetDistance" : 25.4 * mm});
        }
        {
            var Q0;
            Q0=makeQuery(id+"F118.opExtrude","CAP_FACE",FACE,{"disambiguationData":[OSD([sQuery(id+"F117.wireOp",EDGE,"E143.bottom"),sQuery(id+"F117.wireOp",EDGE,"E143.top"),sQuery(id+"F117.wireOp",EDGE,"E143.left"),sQuery(id+"F117.wireOp",EDGE,"E143.right")])],"isStart":false});
            var sketch = newSketch(context, id + "F119", { "sketchPlane" : qUnion([Q0])});
            skCircle(sketch, "E144", {"center": v(-47.76, 0) * mm, "radius": 1.08 * mm});
            skCircle(sketch, "E145", {"center": v(-55.91, 0) * mm, "radius": 1.08 * mm});
            skSolve(sketch);
        }
        {
            var Q0;
            Q0 = qSketchRegion(id + "F119", true);
            extrude(context, id + "F120", {"entities" : qUnion([Q0]), "operationType" : NewBodyOperationType.ADD, "depth" : 7.62 * mm, "offsetDistance" : 25.4 * mm});
        }
        {
            var Q0;
            Q0=makeQuery(id+"F120.opExtrude","CAP_FACE",FACE,{"disambiguationData":[OSD([sQuery(id+"F119.wireOp",EDGE,"E144")])],"isStart":false});
            var sketch = newSketch(context, id + "F121", { "sketchPlane" : qUnion([Q0])});
            skCircle(sketch, "E146", {"center": v(-47.76, 0) * mm, "radius": 0.64 * mm});
            skSolve(sketch);
        }
        {
            var Q0;
            Q0=makeQuery(id+"F120.opExtrude","CAP_FACE",FACE,{"disambiguationData":[OSD([sQuery(id+"F119.wireOp",EDGE,"E145")])],"isStart":false});
            var sketch = newSketch(context, id + "F122", { "sketchPlane" : qUnion([Q0])});
            skCircle(sketch, "E147", {"center": v(-55.91, 0) * mm, "radius": 0.64 * mm});
            skSolve(sketch);
        }
        {
            var Q0;
            Q0=makeQuery(id+"F121.imprint","IMPRINT",FACE,{"disambiguationData":[TD([[makeQuery(id+"F121.imprint","IMPRINT",EDGE,{"derivedFrom":sQuery(id+"F121.wireOp",EDGE,"E146")}),1.0]])]});
            extrude(context, id + "F123", {"entities" : qUnion([Q0]), "operationType" : NewBodyOperationType.ADD, "depth" : 11.43 * mm, "offsetDistance" : 25.4 * mm});
        }
        {
            var Q0;
            Q0=makeQuery(id+"F122.imprint","IMPRINT",FACE,{"disambiguationData":[TD([[makeQuery(id+"F122.imprint","IMPRINT",EDGE,{"derivedFrom":sQuery(id+"F122.wireOp",EDGE,"E147")}),1.0]])]});
            extrude(context, id + "F124", {"entities" : qUnion([Q0]), "operationType" : NewBodyOperationType.ADD, "depth" : 7.62 * mm, "offsetDistance" : 25.4 * mm});
        }
        {
            var Q0;
            Q0=makeQuery(id+"F123.opExtrude","CAP_EDGE",EDGE,{"disambiguationData":[OSD([sQuery(id+"F121.wireOp",EDGE,"E146")])],"isStart":false});
            var Q1;
            Q1=makeQuery(id+"F124.opExtrude","CAP_EDGE",EDGE,{"disambiguationData":[OSD([sQuery(id+"F122.wireOp",EDGE,"E147")])],"isStart":false});
            var Q2;
            Q2=makeQuery(id+"F120.opExtrude","CAP_EDGE",EDGE,{"disambiguationData":[OSD([sQuery(id+"F119.wireOp",EDGE,"E144")])],"isStart":false});
            var Q3;
            Q3=makeQuery(id+"F120.opExtrude","CAP_EDGE",EDGE,{"disambiguationData":[OSD([sQuery(id+"F119.wireOp",EDGE,"E145")])],"isStart":false});
            fillet(context, id + "F125", {"entities" : qUnion([Q0, Q1, Q2, Q3]), "radius" : 0.25 * mm, "tangentPropagation" : true, "allowEdgeOverflow" : false});
        }
        {
            var Q0;
            Q0=makeQuery(id+"F118.opExtrude","CAP_EDGE",EDGE,{"disambiguationData":[OSD([sQuery(id+"F117.wireOp",EDGE,"E143.top")])],"isStart":false});
            var Q1;
            Q1=makeQuery(id+"F118.opExtrude","CAP_EDGE",EDGE,{"disambiguationData":[OSD([sQuery(id+"F117.wireOp",EDGE,"E143.right")])],"isStart":false});
            var Q2;
            Q2=makeQuery(id+"F118.opExtrude","CAP_EDGE",EDGE,{"disambiguationData":[OSD([sQuery(id+"F117.wireOp",EDGE,"E143.bottom")])],"isStart":false});
            var Q3;
            Q3=makeQuery(id+"F118.opExtrude","CAP_EDGE",EDGE,{"disambiguationData":[OSD([sQuery(id+"F117.wireOp",EDGE,"E143.left")])],"isStart":false});
            var Q4;
            Q4=makeQuery(id+"F118.opExtrude","CAP_EDGE",EDGE,{"disambiguationData":[OSD([sQuery(id+"F117.wireOp",EDGE,"E143.top")])],"isStart":true});
            var Q5;
            Q5=makeQuery(id+"F118.opExtrude","CAP_EDGE",EDGE,{"disambiguationData":[OSD([sQuery(id+"F117.wireOp",EDGE,"E143.bottom")])],"isStart":true});
            var Q6;
            Q6=makeQuery(id+"F118.opExtrude","CAP_EDGE",EDGE,{"disambiguationData":[OSD([sQuery(id+"F117.wireOp",EDGE,"E143.right")])],"isStart":true});
            var Q7;
            Q7=makeQuery(id+"F118.opExtrude","CAP_EDGE",EDGE,{"disambiguationData":[OSD([sQuery(id+"F117.wireOp",EDGE,"E143.left")])],"isStart":true});
            var Q8;
            Q8=makeQuery(id+"F114.opExtrude","CAP_EDGE",EDGE,{"disambiguationData":[OSD([sQuery(id+"F113.wireOp",EDGE,"E139.top")])],"isStart":false});
            var Q9;
            Q9=makeQuery(id+"F114.opExtrude","CAP_EDGE",EDGE,{"disambiguationData":[OSD([sQuery(id+"F113.wireOp",EDGE,"E139.left")])],"isStart":false});
            var Q10;
            Q10=makeQuery(id+"F114.opExtrude","CAP_EDGE",EDGE,{"disambiguationData":[OSD([sQuery(id+"F113.wireOp",EDGE,"E139.bottom")])],"isStart":false});
            var Q11;
            Q11=makeQuery(id+"F114.opExtrude","CAP_EDGE",EDGE,{"disambiguationData":[OSD([sQuery(id+"F113.wireOp",EDGE,"E139.right")])],"isStart":false});
            chamfer(context, id + "F126", {"entities" : qUnion([Q0, Q1, Q2, Q3, Q4, Q5, Q6, Q7, Q8, Q9, Q10, Q11]), "width" : 0.64 * mm, "tangentPropagation" : true});
        }
        {
            var Q0;
            {var subQ31=sQuery(id+"F20.wireOp",EDGE,"E11");Q0=makeQuery(id+"F27.boolean.opBoolean","COPY",FACE,{"disambiguationData":[TD([makeQuery(id+"F21.opExtrude","SWEPT_FACE",FACE,{"disambiguationData":[OSD([subQ31])]})])],"derivedFrom":makeQuery(id+"F27.opExtrude","CAP_FACE",FACE,{"disambiguationData":[OSD([sQuery(id+"F26.wireOp",EDGE,"E48.bottom"),sQuery(id+"F26.wireOp",EDGE,"E48.top"),sQuery(id+"F26.wireOp",EDGE,"E48.left"),sQuery(id+"F26.wireOp",EDGE,"E48.right")])],"isStart":true})});}
            var Q1;
            Q1=makeQuery(id+"F27.boolean.opBoolean","COPY",FACE,{"disambiguationData":[TD([makeQuery(id+"F18.opExtrude","SWEPT_FACE",FACE,{"disambiguationData":[OSD([sQuery(id+"F17.wireOp",EDGE,"E10")])]})])],"derivedFrom":makeQuery(id+"F27.opExtrude","CAP_FACE",FACE,{"disambiguationData":[OSD([sQuery(id+"F26.wireOp",EDGE,"E48.bottom"),sQuery(id+"F26.wireOp",EDGE,"E48.top"),sQuery(id+"F26.wireOp",EDGE,"E48.left"),sQuery(id+"F26.wireOp",EDGE,"E48.right")])],"isStart":true})});
            var Q2;
            {var subQ14=sQuery(id+"F22.wireOp",EDGE,"E29");Q2=makeQuery(id+"F25.boolean.opBoolean","COPY",FACE,{"disambiguationData":[TD([makeQuery(id+"F23.opExtrude","SWEPT_FACE",FACE,{"disambiguationData":[OSD([subQ14])]})])],"derivedFrom":makeQuery(id+"F25.opExtrude","CAP_FACE",FACE,{"disambiguationData":[OSD([sQuery(id+"F24.wireOp",EDGE,"E47.bottom"),sQuery(id+"F24.wireOp",EDGE,"E47.top"),sQuery(id+"F24.wireOp",EDGE,"E47.left"),sQuery(id+"F24.wireOp",EDGE,"E47.right")])],"isStart":true})});}
            var Q3;
            Q3=makeQuery(id+"F25.boolean.opBoolean","COPY",FACE,{"disambiguationData":[TD([makeQuery(id+"F16.opExtrude","SWEPT_FACE",FACE,{"disambiguationData":[OSD([sQuery(id+"F15.wireOp",EDGE,"E9")])]})])],"derivedFrom":makeQuery(id+"F25.opExtrude","CAP_FACE",FACE,{"disambiguationData":[OSD([sQuery(id+"F24.wireOp",EDGE,"E47.bottom"),sQuery(id+"F24.wireOp",EDGE,"E47.top"),sQuery(id+"F24.wireOp",EDGE,"E47.left"),sQuery(id+"F24.wireOp",EDGE,"E47.right")])],"isStart":true})});
            shell(context, id + "F127", {"entities" : qUnion([Q0, Q1, Q2, Q3]), "thickness" : 3.8 * mm});
        }
        {
            var Q0;
            Q0=qCreatedBy(makeId("Top.planeOp"),FACE);
            cPlane(context, id + "F128", {"entities" : qUnion([Q0]), "cplaneType" : CPlaneType.OFFSET, "offset" : 58.42 * mm, "oppositeDirection" : true, "width" : 152.4 * mm, "height" : 152.4 * mm});
        }
        {
            var Q0;
            Q0=qCreatedBy(id+"F128.planeOp",FACE);
            var sketch = newSketch(context, id + "F129", { "sketchPlane" : qUnion([Q0])});
            skCircle(sketch, "E148", {"center": v(-9.12, 0) * mm, "radius": 8.9 * mm});
            skSolve(sketch);
        }
        {
            var Q0;
            Q0 = qSketchRegion(id + "F129", true);
            extrude(context, id + "F130", {"entities" : qUnion([Q0]), "oppositeDirection" : true, "depth" : 20.32 * mm, "offsetDistance" : 25.4 * mm});
        }
        {
            var Q0;
            Q0=qCreatedBy(makeId("Front.planeOp"),FACE);
            var sketch = newSketch(context, id + "F131", { "sketchPlane" : qUnion([Q0])});
            skCircle(sketch, "E149", {"center": v(-9.05, -71.35) * mm, "radius": 7.32 * mm});
            skSolve(sketch);
        }
        {
            var Q0;
            Q0 = qSketchRegion(id + "F131", true);
            extrude(context, id + "F132", {"entities" : qUnion([Q0]), "operationType" : NewBodyOperationType.ADD, "depth" : 50.8 * mm, "offsetDistance" : 25.4 * mm});
        }
        {
            var Q0;
            Q0=qCreatedBy(makeId("Front.planeOp"),FACE);
            var sketch = newSketch(context, id + "F133", { "sketchPlane" : qUnion([Q0])});
            skArc(sketch, "E150", {"start": v(-8.96, -78.66) * mm, "mid": v(-2.61, -74.99) * mm, "end": v(-2.71, -67.65) * mm});
            skArc(sketch, "E151", {"start": v(-15.34, -67.65) * mm, "mid": v(-15.4, -75.04) * mm, "end": v(-8.96, -78.66) * mm});
            skLineSegment(sketch, "E152", {"start": v(-15.34, -67.65) * mm, "end": v(-18.87, -67.65) * mm});
            skLineSegment(sketch, "E153", {"start": v(-18.87, -67.65) * mm, "end": v(-19.41, -80.15) * mm});
            skLineSegment(sketch, "E154", {"start": v(-19.41, -80.15) * mm, "end": v(-1.86, -79.79) * mm});
            skLineSegment(sketch, "E155", {"start": v(-1.86, -79.79) * mm, "end": v(3.9, -77.13) * mm});
            skLineSegment(sketch, "E156", {"start": v(3.9, -77.13) * mm, "end": v(1.11, -67.95) * mm});
            skLineSegment(sketch, "E157", {"start": v(1.11, -67.95) * mm, "end": v(-2.71, -67.65) * mm});
            skLineSegment(sketch, "E158", {"start": v(-15.34, -67.65) * mm, "end": v(-15.34, -60.48) * mm});
            skLineSegment(sketch, "E159", {"start": v(-2.71, -67.65) * mm, "end": v(-2.71, -62.65) * mm});
            skFitSpline(sketch, "E160", {"points": [v(-2.71, -62.65) * mm, v(-1.38, -62.88) * mm, v(0.26, -63.2) * mm, v(0.76, -63.29) * mm, v(1.42, -66.87) * mm, v(1.11, -67.95) * mm], "startDerivative": vector(6.52, -0.92) * mm, "endDerivative": vector(-2.46, -4.36) * mm});
            skFitSpline(sketch, "E161", {"points": [v(-15.34, -60.48) * mm, v(-16.3, -60.48) * mm, v(-16.92, -60.34) * mm, v(-17.5, -60.26) * mm, v(-18.11, -60.19) * mm, v(-19.2, -61.78) * mm, v(-18.87, -67.65) * mm], "startDerivative": vector(-7.33, -0.43) * mm, "endDerivative": vector(3.23, -19.4) * mm});
            skSolve(sketch);
        }
        {
            var Q0;
            Q0 = qSketchRegion(id + "F133", true);
            extrude(context, id + "F134", {"entities" : qUnion([Q0]), "operationType" : NewBodyOperationType.REMOVE, "depth" : 127 * mm, "offsetDistance" : 25.4 * mm, "symmetric" : true});
        }
        {
            var Q0;
            Q0=makeQuery(id+"F132.opExtrude","CAP_FACE",FACE,{"disambiguationData":[OSD([sQuery(id+"F131.wireOp",EDGE,"E149")])],"isStart":false});
            var sketch = newSketch(context, id + "F135", { "sketchPlane" : qUnion([Q0])});
            skCircle(sketch, "E162", {"center": v(-8.92, -71.4) * mm, "radius": 4.67 * mm});
            skSolve(sketch);
        }
        {
            var Q0;
            Q0 = qSketchRegion(id + "F135", true);
            extrude(context, id + "F136", {"entities" : qUnion([Q0]), "operationType" : NewBodyOperationType.ADD, "depth" : 25.4 * mm, "offsetDistance" : 25.4 * mm});
        }
        {
            var Q0;
            Q0=makeQuery(id+"F136.opExtrude","CAP_FACE",FACE,{"disambiguationData":[OSD([sQuery(id+"F135.wireOp",EDGE,"E162")])],"isStart":false});
            chamfer(context, id + "F137", {"entities" : qUnion([Q0]), "width" : 2.54 * mm, "tangentPropagation" : true});
        }
        {
            var Q0;
            Q0=makeQuery(id+"F136.opExtrude","CAP_FACE",FACE,{"disambiguationData":[OSD([sQuery(id+"F135.wireOp",EDGE,"E162")])],"isStart":false});
            var sketch = newSketch(context, id + "F138", { "sketchPlane" : qUnion([Q0])});
            skCircle(sketch, "E163", {"center": v(-8.92, -71.4) * mm, "radius": 1.9 * mm});
            skSolve(sketch);
        }
        {
            var Q0;
            Q0 = qSketchRegion(id + "F138", true);
            extrude(context, id + "F139", {"entities" : qUnion([Q0]), "depth" : 0.25 * mm, "offsetDistance" : 25.4 * mm});
        }
        {
            var Q0;
            Q0=qCreatedBy(makeId("Right.planeOp"),FACE);
            var sketch = newSketch(context, id + "F140", { "sketchPlane" : qUnion([Q0])});
            skCircle(sketch, "E164", {"center": v(-28.49, -71.34) * mm, "radius": 3.75 * mm});
            skSolve(sketch);
        }
        {
            var Q0;
            Q0 = qSketchRegion(id + "F140", true);
            extrude(context, id + "F141", {"entities" : qUnion([Q0]), "operationType" : NewBodyOperationType.ADD, "depth" : 17.78 * mm, "offsetDistance" : 25.4 * mm, "symmetric" : true});
        }
        {
            var Q0;
            Q0=qCreatedBy(makeId("Front.planeOp"),FACE);
            cPlane(context, id + "F142", {"entities" : qUnion([Q0]), "cplaneType" : CPlaneType.OFFSET, "offset" : 29.2 * mm, "width" : 152.4 * mm, "height" : 152.4 * mm});
        }
        {
            var Q0;
            Q0=qCreatedBy(id+"F142.planeOp",FACE);
            var sketch = newSketch(context, id + "F143", { "sketchPlane" : qUnion([Q0])});
            skCircle(sketch, "E165", {"center": v(4.7, -71.35) * mm, "radius": 3.68 * mm});
            skSolve(sketch);
        }
        {
            var Q0;
            Q0 = qSketchRegion(id + "F143", true);
            extrude(context, id + "F144", {"entities" : qUnion([Q0]), "operationType" : NewBodyOperationType.ADD, "depth" : 12.7 * mm, "offsetDistance" : 25.4 * mm});
        }
        {
            var Q0;
            Q0=qCreatedBy(id+"F142.planeOp",FACE);
            var sketch = newSketch(context, id + "F145", { "sketchPlane" : qUnion([Q0])});
            skArc(sketch, "E166", {"start": v(4.7, -75.03) * mm, "mid": v(8.38, -71.31) * mm, "end": v(4.64, -67.66) * mm});
            skLineSegment(sketch, "E167", {"start": v(4.64, -67.66) * mm, "end": v(4.8, -67.03) * mm});
            skLineSegment(sketch, "E168", {"start": v(4.8, -67.03) * mm, "end": v(9.84, -67.2) * mm});
            skLineSegment(sketch, "E169", {"start": v(9.84, -67.2) * mm, "end": v(10.74, -73.52) * mm});
            skLineSegment(sketch, "E170", {"start": v(10.74, -73.52) * mm, "end": v(10.42, -76.74) * mm});
            skLineSegment(sketch, "E171", {"start": v(10.42, -76.74) * mm, "end": v(4.9, -76.92) * mm});
            skLineSegment(sketch, "E172", {"start": v(4.9, -76.92) * mm, "end": v(4.7, -75.03) * mm});
            skSolve(sketch);
        }
        {
            var Q0;
            Q0 = qSketchRegion(id + "F145", true);
            extrude(context, id + "F146", {"entities" : qUnion([Q0]), "operationType" : NewBodyOperationType.REMOVE, "oppositeDirection" : true, "depth" : 25.4 * mm, "offsetDistance" : 25.4 * mm, "symmetric" : true});
        }
        {
            var Q0;
            Q0=makeQuery(id+"F144.opExtrude","CAP_FACE",FACE,{"disambiguationData":[OSD([sQuery(id+"F143.wireOp",EDGE,"E165")])],"isStart":false});
            var sketch = newSketch(context, id + "F147", { "sketchPlane" : qUnion([Q0])});
            skCircle(sketch, "E173", {"center": v(4.7, -71.35) * mm, "radius": 2.92 * mm});
            skSolve(sketch);
        }
        {
            var Q0;
            Q0 = qSketchRegion(id + "F147", true);
            extrude(context, id + "F148", {"entities" : qUnion([Q0]), "operationType" : NewBodyOperationType.ADD, "depth" : 7.62 * mm, "offsetDistance" : 25.4 * mm});
        }
        {
            var Q0;
            Q0=makeQuery(id+"F148.opExtrude","CAP_FACE",FACE,{"disambiguationData":[OSD([sQuery(id+"F147.wireOp",EDGE,"E173")])],"isStart":false});
            var sketch = newSketch(context, id + "F149", { "sketchPlane" : qUnion([Q0])});
            skCircle(sketch, "E174", {"center": v(4.7, -71.35) * mm, "radius": 2.29 * mm});
            skSolve(sketch);
        }
        {
            var Q0;
            Q0 = qSketchRegion(id + "F149", true);
            extrude(context, id + "F150", {"entities" : qUnion([Q0]), "operationType" : NewBodyOperationType.ADD, "depth" : 12.7 * mm, "offsetDistance" : 25.4 * mm});
        }
        {
            var Q0;
            Q0=makeQuery(id+"F150.opExtrude","CAP_FACE",FACE,{"disambiguationData":[OSD([sQuery(id+"F149.wireOp",EDGE,"E174")])],"isStart":false});
            var sketch = newSketch(context, id + "F151", { "sketchPlane" : qUnion([Q0])});
            skCircle(sketch, "E175", {"center": v(4.7, -71.35) * mm, "radius": 2.03 * mm});
            skSolve(sketch);
        }
        {
            var Q0;
            Q0 = qSketchRegion(id + "F151", true);
            extrude(context, id + "F152", {"entities" : qUnion([Q0]), "depth" : 0.25 * mm, "offsetDistance" : 25.4 * mm});
        }
        {
            var Q0;
            Q0=makeQuery(id+"F150.opExtrude","CAP_EDGE",EDGE,{"disambiguationData":[OSD([sQuery(id+"F149.wireOp",EDGE,"E174")])],"isStart":false});
            chamfer(context, id + "F153", {"entities" : qUnion([Q0]), "width" : 0.25 * mm, "tangentPropagation" : true});
        }
        {
            var Q0;
            Q0=makeQuery(id+"F148.opExtrude","CAP_EDGE",EDGE,{"disambiguationData":[OSD([sQuery(id+"F147.wireOp",EDGE,"E173")])],"isStart":false});
            var Q1;
            Q1=makeQuery(id+"F146.boolean.opBoolean","COPY",EDGE,{"derivedFrom":makeQuery(id+"F146.opExtrude","CAP_EDGE",EDGE,{"disambiguationData":[OSD([sQuery(id+"F145.wireOp",EDGE,"E166")])],"isStart":true})});
            var Q2;
            Q2=makeQuery(id+"F144.opExtrude","CAP_EDGE",EDGE,{"disambiguationData":[OSD([sQuery(id+"F143.wireOp",EDGE,"E165")])],"isStart":false});
            chamfer(context, id + "F154", {"entities" : qUnion([Q0, Q1, Q2]), "width" : 0.76 * mm, "tangentPropagation" : true});
        }
        {
            var Q0;
            Q0=qCreatedBy(makeId("Front.planeOp"),FACE);
            cPlane(context, id + "F155", {"entities" : qUnion([Q0]), "cplaneType" : CPlaneType.OFFSET, "offset" : 30.48 * mm, "width" : 152.4 * mm, "height" : 152.4 * mm});
        }
        {
            var Q0;
            Q0=qCreatedBy(id+"F155.planeOp",FACE);
            var sketch = newSketch(context, id + "F156", { "sketchPlane" : qUnion([Q0])});
            skLineSegment(sketch, "E176", {"start": v(0, 0) * mm, "end": v(0, 34.3) * mm, "construction": true});
            skLineSegment(sketch, "E177", {"start": v(0, 0) * mm, "end": v(0, -44.45) * mm, "construction": true});
            skLineSegment(sketch, "E178", {"start": v(0, 34.3) * mm, "end": v(0, -44.45) * mm});
            skArc(sketch, "E179", {"start": v(0, 34.3) * mm, "mid": v(-38.6, -5.08) * mm, "end": v(0, -44.45) * mm});
            skSolve(sketch);
        }
        {
            var Q0;
            Q0 = qSketchRegion(id + "F156", true);
            var Q1;
            Q1=sQuery(id+"F156.wireOp",EDGE,"E178");
            revolve(context, id + "F157", {"surfaceOperationType" : NewSurfaceOperationType.NEW, "entities" : qUnion([Q0]), "axis" : qUnion([Q1]), "revolveType" : RevolveType.FULL});
        }
        {
            var Q0;
            Q0=qCreatedBy(id+"F155.planeOp",FACE);
            cPlane(context, id + "F158", {"entities" : qUnion([Q0]), "cplaneType" : CPlaneType.OFFSET, "offset" : 15.24 * mm, "width" : 152.4 * mm, "height" : 152.4 * mm});
        }
        {
            var Q0;
            Q0=qCreatedBy(id+"F158.planeOp",FACE);
            var sketch = newSketch(context, id + "F159", { "sketchPlane" : qUnion([Q0])});
            skLineSegment(sketch, "E180", {"start": v(0, 30.48) * mm, "end": v(0, 0) * mm, "construction": true});
            skLineSegment(sketch, "E181", {"start": v(0, 0) * mm, "end": v(0, -39.37) * mm, "construction": true});
            skLineSegment(sketch, "E182", {"start": v(0, 30.48) * mm, "end": v(0, -39.37) * mm});
            skArc(sketch, "E183", {"start": v(0, 30.48) * mm, "mid": v(-34.93, -4.44) * mm, "end": v(0, -39.37) * mm});
            skSolve(sketch);
        }
        {
            var Q0;
            Q0 = qSketchRegion(id + "F159", true);
            var Q1;
            Q1=sQuery(id+"F159.wireOp",EDGE,"E182");
            revolve(context, id + "F160", {"operationType" : NewBodyOperationType.REMOVE, "surfaceOperationType" : NewSurfaceOperationType.NEW, "entities" : qUnion([Q0]), "axis" : qUnion([Q1]), "revolveType" : RevolveType.FULL, "oppositeDirection" : true});
        }
        {
            var Q0;
            Q0=qCreatedBy(id+"F158.planeOp",FACE);
            var sketch = newSketch(context, id + "F161", { "sketchPlane" : qUnion([Q0])});
            skCircle(sketch, "E184", {"center": v(0, -4.25) * mm, "radius": 34.75 * mm});
            skSolve(sketch);
        }
        {
            var Q0;
            Q0 = qSketchRegion(id + "F161", true);
            extrude(context, id + "F162", {"entities" : qUnion([Q0]), "depth" : 1.52 * mm, "offsetDistance" : 25.4 * mm});
        }
        {
            var Q0;
            Q0=makeQuery(id+"F162.opExtrude","CAP_FACE",FACE,{"disambiguationData":[OSD([sQuery(id+"F161.wireOp",EDGE,"E184")])],"isStart":false});
            var sketch = newSketch(context, id + "F163", { "sketchPlane" : qUnion([Q0])});
            skCircle(sketch, "E185.cCircle", {"center": v(0, -4.25) * mm, "radius": 12.74 * mm, "construction": true});
            skLineSegment(sketch, "E185.0", {"start": v(0.09, 9.54) * mm, "end": v(9.82, 5.44) * mm});
            skLineSegment(sketch, "E185.1", {"start": v(9.82, 5.44) * mm, "end": v(13.8, -4.34) * mm});
            skLineSegment(sketch, "E185.2", {"start": v(13.8, -4.34) * mm, "end": v(9.7, -14.07) * mm});
            skLineSegment(sketch, "E185.3", {"start": v(9.7, -14.07) * mm, "end": v(-0.09, -18.05) * mm});
            skLineSegment(sketch, "E185.4", {"start": v(-0.09, -18.05) * mm, "end": v(-9.82, -13.95) * mm});
            skLineSegment(sketch, "E185.5", {"start": v(-9.82, -13.95) * mm, "end": v(-13.8, -4.17) * mm});
            skLineSegment(sketch, "E185.6", {"start": v(-13.8, -4.17) * mm, "end": v(-9.7, 5.56) * mm});
            skLineSegment(sketch, "E185.7", {"start": v(-9.7, 5.56) * mm, "end": v(0.09, 9.54) * mm});
            skPoint(sketch, "E185.0.midPoint", {"position": v(4.95, 7.49) * mm});
            skLineSegment(sketch, "E186", {"start": v(0.09, 9.54) * mm, "end": v(0.09, 30.5) * mm});
            skLineSegment(sketch, "E187", {"start": v(-0.09, -18.05) * mm, "end": v(-0.09, -39) * mm});
            skLineSegment(sketch, "E188", {"start": v(-9.82, -13.95) * mm, "end": v(-29.83, -22.08) * mm});
            skLineSegment(sketch, "E189", {"start": v(9.7, -14.07) * mm, "end": v(29.6, -22.47) * mm});
            skLineSegment(sketch, "E190", {"start": v(9.82, 5.44) * mm, "end": v(29.83, 13.58) * mm});
            skLineSegment(sketch, "E191", {"start": v(-9.7, 5.56) * mm, "end": v(-29.6, 13.96) * mm});
            skLineSegment(sketch, "E192", {"start": v(-13.8, -4.17) * mm, "end": v(-34.75, -4.17) * mm});
            skLineSegment(sketch, "E193", {"start": v(13.8, -4.34) * mm, "end": v(34.75, -4.34) * mm});
            skLineSegment(sketch, "E194", {"start": v(-0.67, 9.23) * mm, "end": v(-0.67, 30.49) * mm});
            skLineSegment(sketch, "E195", {"start": v(-0.67, 30.49) * mm, "end": v(0.09, 30.5) * mm});
            skLineSegment(sketch, "E196", {"start": v(0.7, 9.29) * mm, "end": v(0.7, 30.49) * mm});
            skLineSegment(sketch, "E197", {"start": v(0.7, 30.49) * mm, "end": v(0.09, 30.5) * mm});
            skLineSegment(sketch, "E198", {"start": v(9.05, 5.76) * mm, "end": v(29.52, 14.09) * mm});
            skLineSegment(sketch, "E199", {"start": v(29.52, 14.09) * mm, "end": v(29.83, 13.58) * mm});
            skLineSegment(sketch, "E200", {"start": v(10.06, 4.84) * mm, "end": v(30.16, 13.01) * mm});
            skLineSegment(sketch, "E201", {"start": v(30.16, 13.01) * mm, "end": v(29.83, 13.58) * mm});
            skLineSegment(sketch, "E202", {"start": v(13.5, -3.62) * mm, "end": v(34.74, -3.62) * mm});
            skLineSegment(sketch, "E203", {"start": v(34.74, -3.62) * mm, "end": v(34.75, -4.34) * mm});
            skLineSegment(sketch, "E204", {"start": v(13.5, -5.04) * mm, "end": v(34.74, -4.97) * mm});
            skLineSegment(sketch, "E205", {"start": v(34.74, -4.97) * mm, "end": v(34.75, -4.34) * mm});
            skLineSegment(sketch, "E206", {"start": v(9.99, -13.36) * mm, "end": v(30, -21.8) * mm});
            skLineSegment(sketch, "E207", {"start": v(30, -21.8) * mm, "end": v(29.6, -22.47) * mm});
            skLineSegment(sketch, "E208", {"start": v(9.7, -14.07) * mm, "end": v(8.87, -14.4) * mm});
            skLineSegment(sketch, "E209", {"start": v(8.87, -14.4) * mm, "end": v(29.25, -23.02) * mm});
            skLineSegment(sketch, "E210", {"start": v(29.25, -23.02) * mm, "end": v(29.6, -22.47) * mm});
            skLineSegment(sketch, "E211", {"start": v(0.7, -17.73) * mm, "end": v(0.84, -39) * mm});
            skLineSegment(sketch, "E212", {"start": v(0.84, -39) * mm, "end": v(-0.09, -39) * mm});
            skLineSegment(sketch, "E213", {"start": v(-0.84, -17.73) * mm, "end": v(-0.84, -39) * mm});
            skLineSegment(sketch, "E214", {"start": v(-0.84, -39) * mm, "end": v(-0.09, -39) * mm});
            skLineSegment(sketch, "E215", {"start": v(-13.44, -5.04) * mm, "end": v(-34.74, -5.2) * mm});
            skLineSegment(sketch, "E216", {"start": v(-34.74, -5.2) * mm, "end": v(-34.75, -4.17) * mm});
            skLineSegment(sketch, "E217", {"start": v(-13.46, -3.37) * mm, "end": v(-34.74, -3.44) * mm});
            skLineSegment(sketch, "E218", {"start": v(-34.74, -3.44) * mm, "end": v(-34.75, -4.17) * mm});
            skLineSegment(sketch, "E219", {"start": v(-10.17, -13.08) * mm, "end": v(-30.3, -21.27) * mm});
            skLineSegment(sketch, "E220", {"start": v(-30.3, -21.27) * mm, "end": v(-29.83, -22.08) * mm});
            skLineSegment(sketch, "E221", {"start": v(-8.94, -14.32) * mm, "end": v(-29.26, -23) * mm});
            skLineSegment(sketch, "E222", {"start": v(-29.26, -23) * mm, "end": v(-29.83, -22.08) * mm});
            skLineSegment(sketch, "E223", {"start": v(-8.66, 5.98) * mm, "end": v(-29.17, 14.63) * mm});
            skLineSegment(sketch, "E224", {"start": v(-29.17, 14.63) * mm, "end": v(-29.6, 13.96) * mm});
            skLineSegment(sketch, "E225", {"start": v(-10.01, 4.8) * mm, "end": v(-30.03, 13.24) * mm});
            skLineSegment(sketch, "E226", {"start": v(-30.03, 13.24) * mm, "end": v(-29.6, 13.96) * mm});
            skLineSegment(sketch, "E227", {"start": v(-0.67, 9.23) * mm, "end": v(0.09, 9.54) * mm});
            skLineSegment(sketch, "E228", {"start": v(0.09, 9.54) * mm, "end": v(0.7, 9.29) * mm});
            skLineSegment(sketch, "E229", {"start": v(9.05, 5.76) * mm, "end": v(9.82, 5.44) * mm});
            skLineSegment(sketch, "E230", {"start": v(9.82, 5.44) * mm, "end": v(10.06, 4.84) * mm});
            skLineSegment(sketch, "E231", {"start": v(13.5, -3.62) * mm, "end": v(13.8, -4.34) * mm});
            skLineSegment(sketch, "E232", {"start": v(13.8, -4.34) * mm, "end": v(13.5, -5.04) * mm});
            skLineSegment(sketch, "E233", {"start": v(9.99, -13.36) * mm, "end": v(9.7, -14.07) * mm});
            skLineSegment(sketch, "E234", {"start": v(0.7, -17.73) * mm, "end": v(-0.09, -18.05) * mm});
            skLineSegment(sketch, "E235", {"start": v(-0.09, -18.05) * mm, "end": v(-0.84, -17.73) * mm});
            skLineSegment(sketch, "E236", {"start": v(-8.94, -14.32) * mm, "end": v(-9.82, -13.95) * mm});
            skLineSegment(sketch, "E237", {"start": v(-10.17, -13.08) * mm, "end": v(-9.82, -13.95) * mm});
            skLineSegment(sketch, "E238", {"start": v(-13.44, -5.04) * mm, "end": v(-13.8, -4.17) * mm});
            skLineSegment(sketch, "E239", {"start": v(-13.8, -4.17) * mm, "end": v(-13.46, -3.37) * mm});
            skLineSegment(sketch, "E240", {"start": v(-10.01, 4.8) * mm, "end": v(-9.7, 5.56) * mm});
            skLineSegment(sketch, "E241", {"start": v(-9.7, 5.56) * mm, "end": v(-8.66, 5.98) * mm});
            skSolve(sketch);
        }
        {
            var Q0;
            Q0 = qSketchRegion(id + "F163", true);
            extrude(context, id + "F164", {"entities" : qUnion([Q0]), "depth" : 0.25 * mm, "offsetDistance" : 25.4 * mm});
        }
        {
            var Q0;
            Q0=makeQuery(id+"F164.opExtrude","CAP_FACE",FACE,{"disambiguationData":[OSD([sQuery(id+"F163.wireOp",EDGE,"E185.0"),sQuery(id+"F163.wireOp",EDGE,"E185.1"),sQuery(id+"F163.wireOp",EDGE,"E185.2"),sQuery(id+"F163.wireOp",EDGE,"E185.3"),sQuery(id+"F163.wireOp",EDGE,"E185.4"),sQuery(id+"F163.wireOp",EDGE,"E185.5"),sQuery(id+"F163.wireOp",EDGE,"E185.6"),sQuery(id+"F163.wireOp",EDGE,"E185.7"),sQuery(id+"F163.wireOp",EDGE,"E194"),sQuery(id+"F163.wireOp",EDGE,"E195"),sQuery(id+"F163.wireOp",EDGE,"E196"),sQuery(id+"F163.wireOp",EDGE,"E197"),sQuery(id+"F163.wireOp",EDGE,"E198"),sQuery(id+"F163.wireOp",EDGE,"E199"),sQuery(id+"F163.wireOp",EDGE,"E200"),sQuery(id+"F163.wireOp",EDGE,"E201"),sQuery(id+"F163.wireOp",EDGE,"E202"),sQuery(id+"F163.wireOp",EDGE,"E203"),sQuery(id+"F163.wireOp",EDGE,"E204"),sQuery(id+"F163.wireOp",EDGE,"E205"),sQuery(id+"F163.wireOp",EDGE,"E206"),sQuery(id+"F163.wireOp",EDGE,"E207"),sQuery(id+"F163.wireOp",EDGE,"E209"),sQuery(id+"F163.wireOp",EDGE,"E210"),sQuery(id+"F163.wireOp",EDGE,"E211"),sQuery(id+"F163.wireOp",EDGE,"E212"),sQuery(id+"F163.wireOp",EDGE,"E213"),sQuery(id+"F163.wireOp",EDGE,"E214"),sQuery(id+"F163.wireOp",EDGE,"E215"),sQuery(id+"F163.wireOp",EDGE,"E216"),sQuery(id+"F163.wireOp",EDGE,"E217"),sQuery(id+"F163.wireOp",EDGE,"E218"),sQuery(id+"F163.wireOp",EDGE,"E219"),sQuery(id+"F163.wireOp",EDGE,"E220"),sQuery(id+"F163.wireOp",EDGE,"E221"),sQuery(id+"F163.wireOp",EDGE,"E222"),sQuery(id+"F163.wireOp",EDGE,"E223"),sQuery(id+"F163.wireOp",EDGE,"E224"),sQuery(id+"F163.wireOp",EDGE,"E225"),sQuery(id+"F163.wireOp",EDGE,"E226")])],"isStart":false});
            shell(context, id + "F165", {"entities" : qUnion([Q0]), "thickness" : 0.03 * mm});
        }
        {
            var Q0;
            Q0=makeQuery(id+"F162.opExtrude","CAP_FACE",FACE,{"disambiguationData":[OSD([sQuery(id+"F161.wireOp",EDGE,"E184")])],"isStart":false});
            var sketch = newSketch(context, id + "F166", { "sketchPlane" : qUnion([Q0])});
            skCircle(sketch, "E242", {"center": v(0, -4.25) * mm, "radius": 34.65 * mm});
            skSolve(sketch);
        }
        {
            var Q0;
            Q0 = qSketchRegion(id + "F166", true);
            extrude(context, id + "F167", {"entities" : qUnion([Q0]), "depth" : 0.76 * mm, "offsetDistance" : 25.4 * mm});
        }
        {
            var Q0;
            Q0=makeQuery(id+"F167.opExtrude","CAP_FACE",FACE,{"disambiguationData":[OSD([sQuery(id+"F166.wireOp",EDGE,"E242")])],"isStart":false});
            var sketch = newSketch(context, id + "F168", { "sketchPlane" : qUnion([Q0])});
            skCircle(sketch, "E243", {"center": v(0, -4.25) * mm, "radius": 34.16 * mm});
            skSolve(sketch);
        }
        {
            var Q0;
            Q0 = qSketchRegion(id + "F168", true);
            extrude(context, id + "F169", {"entities" : qUnion([Q0]), "operationType" : NewBodyOperationType.REMOVE, "oppositeDirection" : true, "depth" : 1.02 * mm, "offsetDistance" : 25.4 * mm});
        }
    });
